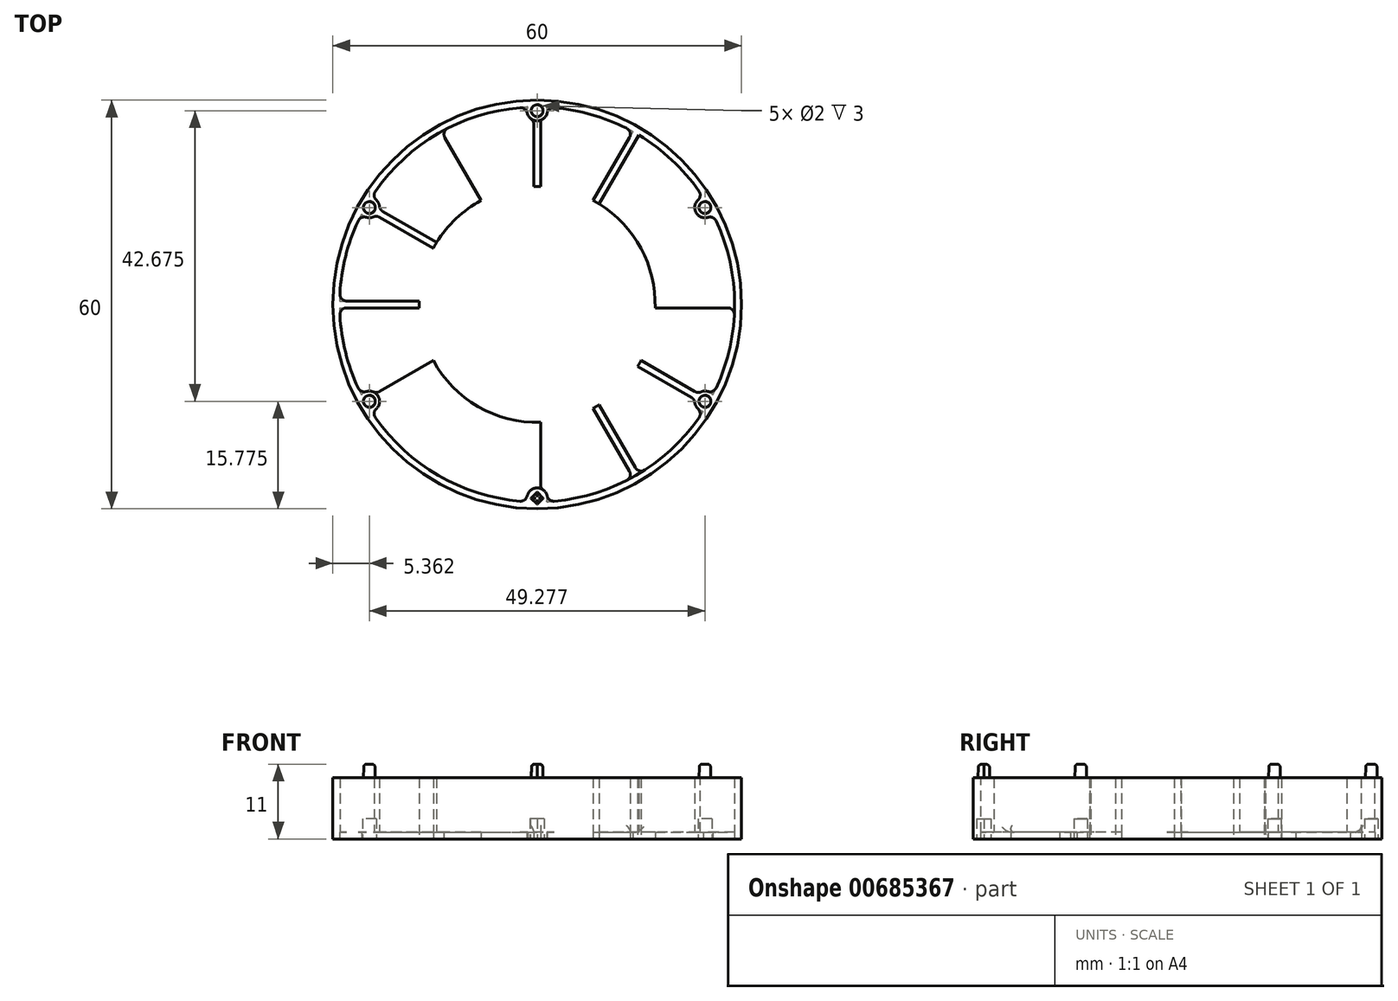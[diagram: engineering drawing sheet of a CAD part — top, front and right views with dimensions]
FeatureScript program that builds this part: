
annotation { "Feature Type Name" : "Feature", "Feature Type Description" : "" }
export const myFeature = defineFeature(function(context is Context, id is Id, definition is map)
    precondition{}
    {
        {
            var Q0;
            Q0=qCreatedBy(makeId("Top.planeOp"),FACE);
            var sketch = newSketch(context, id + "F0", { "sketchPlane" : qUnion([Q0])});
            skCircle(sketch, "E0", {"center": v(0, 0) * mm, "radius": 30 * mm});
            skCircle(sketch, "E1.0", {"center": v(0, 0) * mm, "radius": 29 * mm});
            skLineSegment(sketch, "E2.bottom", {"start": v(14.56, 26.23) * mm, "end": v(15.43, 25.73) * mm});
            skLineSegment(sketch, "E2.top", {"start": v(-15.43, -25.73) * mm, "end": v(-14.56, -26.23) * mm});
            skLineSegment(sketch, "E2.left", {"start": v(14.56, 26.23) * mm, "end": v(-15.43, -25.73) * mm});
            skLineSegment(sketch, "E2.right", {"start": v(15.43, 25.73) * mm, "end": v(-14.56, -26.23) * mm});
            skLineSegment(sketch, "E3.bottom", {"start": v(25.73, 15.43) * mm, "end": v(26.23, 14.56) * mm});
            skLineSegment(sketch, "E3.top", {"start": v(-26.23, -14.56) * mm, "end": v(-25.73, -15.43) * mm});
            skLineSegment(sketch, "E3.left", {"start": v(25.73, 15.43) * mm, "end": v(-26.23, -14.56) * mm});
            skLineSegment(sketch, "E3.right", {"start": v(26.23, 14.56) * mm, "end": v(-25.73, -15.43) * mm});
            skLineSegment(sketch, "E4", {"start": v(-38.35, 0) * mm, "end": v(39.17, 0) * mm, "construction": true});
            skLineSegment(sketch, "E5", {"start": v(0, 42.5) * mm, "end": v(0, -42.47) * mm, "construction": true});
            skLineSegment(sketch, "E6.bottom", {"start": v(-30, 0.5) * mm, "end": v(30, 0.5) * mm});
            skLineSegment(sketch, "E6.top", {"start": v(-30, -0.5) * mm, "end": v(30, -0.5) * mm});
            skLineSegment(sketch, "E6.left", {"start": v(-30, 0.5) * mm, "end": v(-30, -0.5) * mm});
            skLineSegment(sketch, "E6.right", {"start": v(30, 0.5) * mm, "end": v(30, -0.5) * mm});
            skLineSegment(sketch, "E7.bottom", {"start": v(-25.73, 15.43) * mm, "end": v(26.23, -14.56) * mm});
            skLineSegment(sketch, "E7.top", {"start": v(-26.23, 14.56) * mm, "end": v(25.73, -15.43) * mm});
            skLineSegment(sketch, "E7.left", {"start": v(-25.73, 15.43) * mm, "end": v(-26.23, 14.56) * mm});
            skLineSegment(sketch, "E7.right", {"start": v(26.23, -14.56) * mm, "end": v(25.73, -15.43) * mm});
            skLineSegment(sketch, "E8.bottom", {"start": v(-0.5, 30) * mm, "end": v(0.5, 30) * mm});
            skLineSegment(sketch, "E8.top", {"start": v(-0.5, -30) * mm, "end": v(0.5, -30) * mm});
            skLineSegment(sketch, "E8.left", {"start": v(-0.5, 30) * mm, "end": v(-0.5, -30) * mm});
            skLineSegment(sketch, "E8.right", {"start": v(0.5, 30) * mm, "end": v(0.5, -30) * mm});
            skLineSegment(sketch, "E9.bottom", {"start": v(-15.43, 25.73) * mm, "end": v(-14.56, 26.23) * mm});
            skLineSegment(sketch, "E9.top", {"start": v(14.56, -26.23) * mm, "end": v(15.43, -25.73) * mm});
            skLineSegment(sketch, "E9.left", {"start": v(-15.43, 25.73) * mm, "end": v(14.56, -26.23) * mm});
            skLineSegment(sketch, "E9.right", {"start": v(-14.56, 26.23) * mm, "end": v(15.43, -25.73) * mm});
            skCircle(sketch, "E10", {"center": v(0, 0) * mm, "radius": 17.33 * mm});
            skSolve(sketch);
        }
        {
            var Q0;
            Q0=qCreatedBy(makeId("Top.planeOp"),FACE);
            var sketch = newSketch(context, id + "F1", { "sketchPlane" : qUnion([Q0])});
            skCircle(sketch, "E11", {"center": v(0, 0) * mm, "radius": 30 * mm});
            skCircle(sketch, "E12", {"center": v(0, 0) * mm, "radius": 29 * mm});
            skSolve(sketch);
        }
        {
            var Q0;
            Q0=makeQuery(id+"F1.imprint","IMPRINT",FACE,{"disambiguationData":[TD([[makeQuery(id+"F1.imprint","IMPRINT",EDGE,{"derivedFrom":sQuery(id+"F1.wireOp",EDGE,"E11")}),1.0]])]});
            extrude(context, id + "F2", {"entities" : qUnion([Q0]), "depth" : 9 * mm, "offsetDistance" : 25 * mm});
        }
        {
            var Q0;
            {var subQ0=sQuery(id+"F0.wireOp",EDGE,"E7.bottom");var subQ1=sQuery(id+"F0.wireOp",EDGE,"E1.0");var subQ2=makeQuery(id+"F0.imprint","INTERSECT",VERTEX,{"disambiguationData":[OD(0.0)],"derivedFrom":[subQ1,subQ0]});Q0=makeQuery(id+"F0.imprint","IMPRINT",FACE,{"disambiguationData":[TD([[makeQuery(id+"F0.imprint","IMPRINT",EDGE,{"disambiguationData":[TD([[subQ2,-1.0]])],"derivedFrom":subQ1}),1.0]])]});}
            var Q1;
            {var subQ0=sQuery(id+"F0.wireOp",EDGE,"E2.right");var subQ1=sQuery(id+"F0.wireOp",EDGE,"E1.0");var subQ2=makeQuery(id+"F0.imprint","INTERSECT",VERTEX,{"disambiguationData":[OD(0.0)],"derivedFrom":[subQ1,subQ0]});Q1=makeQuery(id+"F0.imprint","IMPRINT",FACE,{"disambiguationData":[TD([[makeQuery(id+"F0.imprint","IMPRINT",EDGE,{"disambiguationData":[TD([[subQ2,-1.0]])],"derivedFrom":subQ1}),1.0]])]});}
            var Q2;
            {var subQ0=sQuery(id+"F0.wireOp",EDGE,"E7.top");var subQ1=sQuery(id+"F0.wireOp",EDGE,"E1.0");var subQ2=makeQuery(id+"F0.imprint","INTERSECT",VERTEX,{"disambiguationData":[OD(1.0)],"derivedFrom":[subQ1,subQ0]});Q2=makeQuery(id+"F0.imprint","IMPRINT",FACE,{"disambiguationData":[TD([[makeQuery(id+"F0.imprint","IMPRINT",EDGE,{"disambiguationData":[TD([[subQ2,-1.0]])],"derivedFrom":subQ1}),1.0]])]});}
            var Q3;
            {var subQ0=sQuery(id+"F0.wireOp",EDGE,"E6.bottom");var subQ1=sQuery(id+"F0.wireOp",EDGE,"E1.0");var subQ2=makeQuery(id+"F0.imprint","INTERSECT",VERTEX,{"disambiguationData":[OD(1.0)],"derivedFrom":[subQ1,subQ0]});Q3=makeQuery(id+"F0.imprint","IMPRINT",FACE,{"disambiguationData":[TD([[makeQuery(id+"F0.imprint","IMPRINT",EDGE,{"disambiguationData":[TD([[subQ2,-1.0]])],"derivedFrom":subQ1}),1.0]])]});}
            extrude(context, id + "F3", {"entities" : qUnion([Q0, Q1, Q2, Q3]), "operationType" : NewBodyOperationType.ADD, "depth" : 9 * mm, "offsetDistance" : 25 * mm});
        }
        {
            var Q0;
            Q0=makeQuery(id+"F1.imprint","IMPRINT",FACE,{"disambiguationData":[TD([[makeQuery(id+"F1.imprint","IMPRINT",EDGE,{"derivedFrom":sQuery(id+"F1.wireOp",EDGE,"E11")}),1.0]])]});
            var Q1;
            Q1=makeQuery(id+"F1.imprint","IMPRINT",FACE,{"disambiguationData":[TD([[makeQuery(id+"F1.imprint","IMPRINT",EDGE,{"derivedFrom":sQuery(id+"F1.wireOp",EDGE,"E12")}),1.0]])]});
            extrude(context, id + "F4", {"entities" : qUnion([Q0, Q1]), "operationType" : NewBodyOperationType.ADD, "depth" : 1 * mm, "offsetDistance" : 25 * mm});
        }
        {
            var Q0;
            {var subQ0=sQuery(id+"F0.wireOp",EDGE,"E8.right");var subQ1=sQuery(id+"F0.wireOp",EDGE,"E1.0");var subQ2=makeQuery(id+"F0.imprint","INTERSECT",VERTEX,{"disambiguationData":[OD(1.0)],"derivedFrom":[subQ1,subQ0]});Q0=makeQuery(id+"F0.imprint","IMPRINT",FACE,{"disambiguationData":[TD([[makeQuery(id+"F0.imprint","IMPRINT",EDGE,{"disambiguationData":[TD([[subQ2,-1.0]])],"derivedFrom":subQ1}),1.0]])]});}
            var Q1;
            {var subQ0=sQuery(id+"F0.wireOp",EDGE,"E9.right");var subQ1=sQuery(id+"F0.wireOp",EDGE,"E1.0");var subQ2=makeQuery(id+"F0.imprint","INTERSECT",VERTEX,{"disambiguationData":[OD(1.0)],"derivedFrom":[subQ1,subQ0]});Q1=makeQuery(id+"F0.imprint","IMPRINT",FACE,{"disambiguationData":[TD([[makeQuery(id+"F0.imprint","IMPRINT",EDGE,{"disambiguationData":[TD([[subQ2,-1.0]])],"derivedFrom":subQ1}),1.0]])]});}
            var Q2;
            {var subQ0=sQuery(id+"F0.wireOp",EDGE,"E7.bottom");var subQ1=sQuery(id+"F0.wireOp",EDGE,"E1.0");var subQ2=makeQuery(id+"F0.imprint","INTERSECT",VERTEX,{"disambiguationData":[OD(1.0)],"derivedFrom":[subQ1,subQ0]});Q2=makeQuery(id+"F0.imprint","IMPRINT",FACE,{"disambiguationData":[TD([[makeQuery(id+"F0.imprint","IMPRINT",EDGE,{"disambiguationData":[TD([[subQ2,-1.0]])],"derivedFrom":subQ1}),1.0]])]});}
            var Q3;
            {var subQ0=sQuery(id+"F0.wireOp",EDGE,"E2.left");var subQ1=sQuery(id+"F0.wireOp",EDGE,"E1.0");var subQ2=makeQuery(id+"F0.imprint","INTERSECT",VERTEX,{"disambiguationData":[OD(0.0)],"derivedFrom":[subQ1,subQ0]});Q3=makeQuery(id+"F0.imprint","IMPRINT",FACE,{"disambiguationData":[TD([[makeQuery(id+"F0.imprint","IMPRINT",EDGE,{"disambiguationData":[TD([[subQ2,-1.0]])],"derivedFrom":subQ1}),1.0]])]});}
            var Q4;
            {var subQ0=sQuery(id+"F0.wireOp",EDGE,"E8.left");var subQ1=sQuery(id+"F0.wireOp",EDGE,"E1.0");var subQ2=makeQuery(id+"F0.imprint","INTERSECT",VERTEX,{"disambiguationData":[OD(0.0)],"derivedFrom":[subQ1,subQ0]});Q4=makeQuery(id+"F0.imprint","IMPRINT",FACE,{"disambiguationData":[TD([[makeQuery(id+"F0.imprint","IMPRINT",EDGE,{"disambiguationData":[TD([[subQ2,-1.0]])],"derivedFrom":subQ1}),1.0]])]});}
            var Q5;
            {var subQ0=sQuery(id+"F0.wireOp",EDGE,"E7.top");var subQ1=sQuery(id+"F0.wireOp",EDGE,"E1.0");var subQ2=makeQuery(id+"F0.imprint","INTERSECT",VERTEX,{"disambiguationData":[OD(0.0)],"derivedFrom":[subQ1,subQ0]});Q5=makeQuery(id+"F0.imprint","IMPRINT",FACE,{"disambiguationData":[TD([[makeQuery(id+"F0.imprint","IMPRINT",EDGE,{"disambiguationData":[TD([[subQ2,-1.0]])],"derivedFrom":subQ1}),1.0]])]});}
            var Q6;
            {var subQ0=sQuery(id+"F0.wireOp",EDGE,"E6.top");var subQ1=sQuery(id+"F0.wireOp",EDGE,"E1.0");var subQ2=makeQuery(id+"F0.imprint","INTERSECT",VERTEX,{"disambiguationData":[OD(0.0)],"derivedFrom":[subQ1,subQ0]});Q6=makeQuery(id+"F0.imprint","IMPRINT",FACE,{"disambiguationData":[TD([[makeQuery(id+"F0.imprint","IMPRINT",EDGE,{"disambiguationData":[TD([[subQ2,-1.0]])],"derivedFrom":subQ1}),1.0]])]});}
            extrude(context, id + "F5", {"entities" : qUnion([Q0, Q1, Q2, Q3, Q4, Q5, Q6]), "operationType" : NewBodyOperationType.REMOVE, "depth" : 1 * mm, "offsetDistance" : 25 * mm});
        }
        {
            var Q0;
            Q0=qCreatedBy(makeId("Top.planeOp"),FACE);
            var sketch = newSketch(context, id + "F6", { "sketchPlane" : qUnion([Q0])});
            skCircle(sketch, "E13", {"center": v(0, 0) * mm, "radius": 28.45 * mm});
            skLineSegment(sketch, "E14", {"start": v(0, 28.45) * mm, "end": v(0, -28.45) * mm, "construction": true});
            skLineSegment(sketch, "E15", {"start": v(24.64, 14.22) * mm, "end": v(0, 0) * mm, "construction": true});
            skLineSegment(sketch, "E16", {"start": v(14.23, 24.64) * mm, "end": v(0, 0) * mm, "construction": true});
            skLineSegment(sketch, "E17", {"start": v(0, 0) * mm, "end": v(28.45, 0) * mm, "construction": true});
            skLineSegment(sketch, "E18", {"start": v(0, 0) * mm, "end": v(24.64, -14.22) * mm, "construction": true});
            skLineSegment(sketch, "E19", {"start": v(0, 0) * mm, "end": v(14.23, -24.64) * mm, "construction": true});
            skLineSegment(sketch, "E20", {"start": v(0, 0) * mm, "end": v(-14.23, 24.64) * mm, "construction": true});
            skLineSegment(sketch, "E21", {"start": v(0, 0) * mm, "end": v(-24.64, 14.22) * mm, "construction": true});
            skLineSegment(sketch, "E22", {"start": v(0, 0) * mm, "end": v(-28.45, 0) * mm, "construction": true});
            skLineSegment(sketch, "E23", {"start": v(0, 0) * mm, "end": v(-24.64, -14.23) * mm, "construction": true});
            skLineSegment(sketch, "E24", {"start": v(0, 0) * mm, "end": v(-14.22, -24.64) * mm, "construction": true});
            skCircle(sketch, "E25", {"center": v(0, 28.45) * mm, "radius": 1.5 * mm});
            skCircle(sketch, "E26", {"center": v(24.64, 14.22) * mm, "radius": 1.5 * mm});
            skCircle(sketch, "E27", {"center": v(24.64, -14.22) * mm, "radius": 1.5 * mm});
            skCircle(sketch, "E28", {"center": v(0, -28.45) * mm, "radius": 1.5 * mm});
            skCircle(sketch, "E29", {"center": v(-24.64, -14.23) * mm, "radius": 1.5 * mm});
            skCircle(sketch, "E30", {"center": v(-24.64, 14.22) * mm, "radius": 1.5 * mm});
            skCircle(sketch, "E31", {"center": v(-24.64, 14.22) * mm, "radius": 1 * mm});
            skCircle(sketch, "E32", {"center": v(0, 28.45) * mm, "radius": 1 * mm});
            skCircle(sketch, "E33", {"center": v(24.64, 14.22) * mm, "radius": 1 * mm});
            skCircle(sketch, "E34", {"center": v(24.64, -14.22) * mm, "radius": 1 * mm});
            skCircle(sketch, "E35", {"center": v(-24.64, -14.23) * mm, "radius": 1 * mm});
            skLineSegment(sketch, "E36.bottom", {"start": v(1.06, -28.45) * mm, "end": v(0, -29.51) * mm});
            skLineSegment(sketch, "E36.top", {"start": v(0, -27.39) * mm, "end": v(-1.06, -28.45) * mm});
            skLineSegment(sketch, "E36.left", {"start": v(1.06, -28.45) * mm, "end": v(0, -27.39) * mm});
            skLineSegment(sketch, "E36.right", {"start": v(0, -29.51) * mm, "end": v(-1.06, -28.45) * mm});
            skSolve(sketch);
        }
        {
            var Q0;
            {var subQ0=sQuery(id+"F6.wireOp",EDGE,"E30");var subQ1=sQuery(id+"F6.wireOp",EDGE,"E13");var subQ2=makeQuery(id+"F6.imprint","INTERSECT",VERTEX,{"disambiguationData":[OD(0.0)],"derivedFrom":[subQ1,subQ0]});Q0=makeQuery(id+"F6.imprint","IMPRINT",FACE,{"disambiguationData":[TD([[makeQuery(id+"F6.imprint","IMPRINT",EDGE,{"disambiguationData":[TD([[subQ2,-1.0]])],"derivedFrom":subQ1}),1.0]])]});}
            var Q1;
            {var subQ0=sQuery(id+"F6.wireOp",EDGE,"E30");var subQ1=sQuery(id+"F6.wireOp",EDGE,"E13");var subQ2=makeQuery(id+"F6.imprint","INTERSECT",VERTEX,{"disambiguationData":[OD(0.0)],"derivedFrom":[subQ1,subQ0]});Q1=makeQuery(id+"F6.imprint","IMPRINT",FACE,{"disambiguationData":[TD([[makeQuery(id+"F6.imprint","IMPRINT",EDGE,{"disambiguationData":[TD([[subQ2,-1.0]])],"derivedFrom":subQ1}),-1.0]])]});}
            var Q2;
            {var subQ0=sQuery(id+"F6.wireOp",EDGE,"E25");var subQ1=sQuery(id+"F6.wireOp",EDGE,"E13");var subQ2=makeQuery(id+"F6.imprint","INTERSECT",VERTEX,{"disambiguationData":[OD(0.0)],"derivedFrom":[subQ1,subQ0]});Q2=makeQuery(id+"F6.imprint","IMPRINT",FACE,{"disambiguationData":[TD([[makeQuery(id+"F6.imprint","IMPRINT",EDGE,{"disambiguationData":[TD([[subQ2,-1.0]])],"derivedFrom":subQ1}),1.0]])]});}
            var Q3;
            {var subQ0=sQuery(id+"F6.wireOp",EDGE,"E25");var subQ1=sQuery(id+"F6.wireOp",EDGE,"E13");var subQ2=makeQuery(id+"F6.imprint","INTERSECT",VERTEX,{"disambiguationData":[OD(0.0)],"derivedFrom":[subQ1,subQ0]});Q3=makeQuery(id+"F6.imprint","IMPRINT",FACE,{"disambiguationData":[TD([[makeQuery(id+"F6.imprint","IMPRINT",EDGE,{"disambiguationData":[TD([[subQ2,-1.0]])],"derivedFrom":subQ1}),-1.0]])]});}
            var Q4;
            {var subQ0=sQuery(id+"F6.wireOp",EDGE,"E26");var subQ1=sQuery(id+"F6.wireOp",EDGE,"E13");var subQ2=makeQuery(id+"F6.imprint","INTERSECT",VERTEX,{"disambiguationData":[OD(0.0)],"derivedFrom":[subQ1,subQ0]});Q4=makeQuery(id+"F6.imprint","IMPRINT",FACE,{"disambiguationData":[TD([[makeQuery(id+"F6.imprint","IMPRINT",EDGE,{"disambiguationData":[TD([[subQ2,-1.0]])],"derivedFrom":subQ1}),-1.0]])]});}
            var Q5;
            {var subQ0=sQuery(id+"F6.wireOp",EDGE,"E26");var subQ1=sQuery(id+"F6.wireOp",EDGE,"E13");var subQ2=makeQuery(id+"F6.imprint","INTERSECT",VERTEX,{"disambiguationData":[OD(0.0)],"derivedFrom":[subQ1,subQ0]});Q5=makeQuery(id+"F6.imprint","IMPRINT",FACE,{"disambiguationData":[TD([[makeQuery(id+"F6.imprint","IMPRINT",EDGE,{"disambiguationData":[TD([[subQ2,-1.0]])],"derivedFrom":subQ1}),1.0]])]});}
            var Q6;
            {var subQ0=sQuery(id+"F6.wireOp",EDGE,"E29");var subQ1=sQuery(id+"F6.wireOp",EDGE,"E13");var subQ2=makeQuery(id+"F6.imprint","INTERSECT",VERTEX,{"disambiguationData":[OD(0.0)],"derivedFrom":[subQ1,subQ0]});Q6=makeQuery(id+"F6.imprint","IMPRINT",FACE,{"disambiguationData":[TD([[makeQuery(id+"F6.imprint","IMPRINT",EDGE,{"disambiguationData":[TD([[subQ2,-1.0]])],"derivedFrom":subQ1}),1.0]])]});}
            var Q7;
            {var subQ0=sQuery(id+"F6.wireOp",EDGE,"E29");var subQ1=sQuery(id+"F6.wireOp",EDGE,"E13");var subQ2=makeQuery(id+"F6.imprint","INTERSECT",VERTEX,{"disambiguationData":[OD(0.0)],"derivedFrom":[subQ1,subQ0]});Q7=makeQuery(id+"F6.imprint","IMPRINT",FACE,{"disambiguationData":[TD([[makeQuery(id+"F6.imprint","IMPRINT",EDGE,{"disambiguationData":[TD([[subQ2,-1.0]])],"derivedFrom":subQ1}),-1.0]])]});}
            var Q8;
            {var subQ3=sQuery(id+"F6.wireOp",EDGE,"E13");var subQ5=sQuery(id+"F6.wireOp",EDGE,"E28");var subQ6=makeQuery(id+"F6.imprint","INTERSECT",VERTEX,{"disambiguationData":[OD(0.0)],"derivedFrom":[subQ3,subQ5]});Q8=makeQuery(id+"F6.imprint","IMPRINT",FACE,{"disambiguationData":[TD([[makeQuery(id+"F6.imprint","IMPRINT",EDGE,{"disambiguationData":[TD([[subQ6,-1.0]])],"derivedFrom":subQ3}),1.0]])]});}
            var Q9;
            {var subQ6=sQuery(id+"F6.wireOp",EDGE,"E36.bottom");Q9=makeQuery(id+"F6.imprint","IMPRINT",FACE,{"disambiguationData":[TD([[makeQuery(id+"F6.imprint","IMPRINT",EDGE,{"derivedFrom":subQ6}),1.0]])]});}
            var Q10;
            {var subQ0=sQuery(id+"F6.wireOp",EDGE,"E27");var subQ1=sQuery(id+"F6.wireOp",EDGE,"E13");var subQ2=makeQuery(id+"F6.imprint","INTERSECT",VERTEX,{"disambiguationData":[OD(0.0)],"derivedFrom":[subQ1,subQ0]});Q10=makeQuery(id+"F6.imprint","IMPRINT",FACE,{"disambiguationData":[TD([[makeQuery(id+"F6.imprint","IMPRINT",EDGE,{"disambiguationData":[TD([[subQ2,-1.0]])],"derivedFrom":subQ1}),-1.0]])]});}
            var Q11;
            {var subQ0=sQuery(id+"F6.wireOp",EDGE,"E27");var subQ1=sQuery(id+"F6.wireOp",EDGE,"E13");var subQ2=makeQuery(id+"F6.imprint","INTERSECT",VERTEX,{"disambiguationData":[OD(0.0)],"derivedFrom":[subQ1,subQ0]});Q11=makeQuery(id+"F6.imprint","IMPRINT",FACE,{"disambiguationData":[TD([[makeQuery(id+"F6.imprint","IMPRINT",EDGE,{"disambiguationData":[TD([[subQ2,-1.0]])],"derivedFrom":subQ1}),1.0]])]});}
            var Q12;
            {var subQ0=sQuery(id+"F6.wireOp",EDGE,"E31");var subQ1=sQuery(id+"F6.wireOp",EDGE,"E13");var subQ2=makeQuery(id+"F6.imprint","INTERSECT",VERTEX,{"disambiguationData":[OD(0.0)],"derivedFrom":[subQ1,subQ0]});Q12=makeQuery(id+"F6.imprint","IMPRINT",FACE,{"disambiguationData":[TD([[makeQuery(id+"F6.imprint","IMPRINT",EDGE,{"disambiguationData":[TD([[subQ2,-1.0]])],"derivedFrom":subQ1}),1.0]])]});}
            var Q13;
            {var subQ0=sQuery(id+"F6.wireOp",EDGE,"E31");var subQ1=sQuery(id+"F6.wireOp",EDGE,"E13");var subQ2=makeQuery(id+"F6.imprint","INTERSECT",VERTEX,{"disambiguationData":[OD(0.0)],"derivedFrom":[subQ1,subQ0]});Q13=makeQuery(id+"F6.imprint","IMPRINT",FACE,{"disambiguationData":[TD([[makeQuery(id+"F6.imprint","IMPRINT",EDGE,{"disambiguationData":[TD([[subQ2,-1.0]])],"derivedFrom":subQ1}),-1.0]])]});}
            var Q14;
            {var subQ0=sQuery(id+"F6.wireOp",EDGE,"E32");var subQ1=sQuery(id+"F6.wireOp",EDGE,"E13");var subQ2=makeQuery(id+"F6.imprint","INTERSECT",VERTEX,{"disambiguationData":[OD(0.0)],"derivedFrom":[subQ1,subQ0]});Q14=makeQuery(id+"F6.imprint","IMPRINT",FACE,{"disambiguationData":[TD([[makeQuery(id+"F6.imprint","IMPRINT",EDGE,{"disambiguationData":[TD([[subQ2,-1.0]])],"derivedFrom":subQ1}),-1.0]])]});}
            var Q15;
            {var subQ0=sQuery(id+"F6.wireOp",EDGE,"E32");var subQ1=sQuery(id+"F6.wireOp",EDGE,"E13");var subQ2=makeQuery(id+"F6.imprint","INTERSECT",VERTEX,{"disambiguationData":[OD(0.0)],"derivedFrom":[subQ1,subQ0]});Q15=makeQuery(id+"F6.imprint","IMPRINT",FACE,{"disambiguationData":[TD([[makeQuery(id+"F6.imprint","IMPRINT",EDGE,{"disambiguationData":[TD([[subQ2,-1.0]])],"derivedFrom":subQ1}),1.0]])]});}
            var Q16;
            {var subQ0=sQuery(id+"F6.wireOp",EDGE,"E33");var subQ1=sQuery(id+"F6.wireOp",EDGE,"E13");var subQ2=makeQuery(id+"F6.imprint","INTERSECT",VERTEX,{"disambiguationData":[OD(0.0)],"derivedFrom":[subQ1,subQ0]});Q16=makeQuery(id+"F6.imprint","IMPRINT",FACE,{"disambiguationData":[TD([[makeQuery(id+"F6.imprint","IMPRINT",EDGE,{"disambiguationData":[TD([[subQ2,-1.0]])],"derivedFrom":subQ1}),-1.0]])]});}
            var Q17;
            {var subQ0=sQuery(id+"F6.wireOp",EDGE,"E33");var subQ1=sQuery(id+"F6.wireOp",EDGE,"E13");var subQ2=makeQuery(id+"F6.imprint","INTERSECT",VERTEX,{"disambiguationData":[OD(0.0)],"derivedFrom":[subQ1,subQ0]});Q17=makeQuery(id+"F6.imprint","IMPRINT",FACE,{"disambiguationData":[TD([[makeQuery(id+"F6.imprint","IMPRINT",EDGE,{"disambiguationData":[TD([[subQ2,-1.0]])],"derivedFrom":subQ1}),1.0]])]});}
            var Q18;
            {var subQ0=sQuery(id+"F6.wireOp",EDGE,"E34");var subQ1=sQuery(id+"F6.wireOp",EDGE,"E13");var subQ2=makeQuery(id+"F6.imprint","INTERSECT",VERTEX,{"disambiguationData":[OD(0.0)],"derivedFrom":[subQ1,subQ0]});Q18=makeQuery(id+"F6.imprint","IMPRINT",FACE,{"disambiguationData":[TD([[makeQuery(id+"F6.imprint","IMPRINT",EDGE,{"disambiguationData":[TD([[subQ2,-1.0]])],"derivedFrom":subQ1}),-1.0]])]});}
            var Q19;
            {var subQ0=sQuery(id+"F6.wireOp",EDGE,"E34");var subQ1=sQuery(id+"F6.wireOp",EDGE,"E13");var subQ2=makeQuery(id+"F6.imprint","INTERSECT",VERTEX,{"disambiguationData":[OD(0.0)],"derivedFrom":[subQ1,subQ0]});Q19=makeQuery(id+"F6.imprint","IMPRINT",FACE,{"disambiguationData":[TD([[makeQuery(id+"F6.imprint","IMPRINT",EDGE,{"disambiguationData":[TD([[subQ2,-1.0]])],"derivedFrom":subQ1}),1.0]])]});}
            var Q20;
            {var subQ1=sQuery(id+"F6.wireOp",EDGE,"E36.bottom");Q20=makeQuery(id+"F6.imprint","IMPRINT",FACE,{"disambiguationData":[TD([[makeQuery(id+"F6.imprint","IMPRINT",EDGE,{"derivedFrom":subQ1}),-1.0]])]});}
            var Q21;
            {var subQ0=sQuery(id+"F6.wireOp",EDGE,"E35");var subQ1=sQuery(id+"F6.wireOp",EDGE,"E13");var subQ2=makeQuery(id+"F6.imprint","INTERSECT",VERTEX,{"disambiguationData":[OD(0.0)],"derivedFrom":[subQ1,subQ0]});Q21=makeQuery(id+"F6.imprint","IMPRINT",FACE,{"disambiguationData":[TD([[makeQuery(id+"F6.imprint","IMPRINT",EDGE,{"disambiguationData":[TD([[subQ2,-1.0]])],"derivedFrom":subQ1}),-1.0]])]});}
            var Q22;
            {var subQ0=sQuery(id+"F6.wireOp",EDGE,"E35");var subQ1=sQuery(id+"F6.wireOp",EDGE,"E13");var subQ2=makeQuery(id+"F6.imprint","INTERSECT",VERTEX,{"disambiguationData":[OD(0.0)],"derivedFrom":[subQ1,subQ0]});Q22=makeQuery(id+"F6.imprint","IMPRINT",FACE,{"disambiguationData":[TD([[makeQuery(id+"F6.imprint","IMPRINT",EDGE,{"disambiguationData":[TD([[subQ2,-1.0]])],"derivedFrom":subQ1}),1.0]])]});}
            var Q23;
            {var subQ0=sQuery(id+"F6.wireOp",EDGE,"E36.top");var subQ1=sQuery(id+"F6.wireOp",EDGE,"E13");var subQ2=makeQuery(id+"F6.imprint","INTERSECT",VERTEX,{"derivedFrom":[subQ1,subQ0]});Q23=makeQuery(id+"F6.imprint","IMPRINT",FACE,{"disambiguationData":[TD([[makeQuery(id+"F6.imprint","IMPRINT",EDGE,{"disambiguationData":[TD([[subQ2,-1.0]])],"derivedFrom":subQ1}),1.0]])]});}
            extrude(context, id + "F7", {"entities" : qUnion([Q0, Q1, Q2, Q3, Q4, Q5, Q6, Q7, Q8, Q9, Q10, Q11, Q12, Q13, Q14, Q15, Q16, Q17, Q18, Q19, Q20, Q21, Q22, Q23]), "operationType" : NewBodyOperationType.ADD, "depth" : 9 * mm, "offsetDistance" : 25 * mm});
        }
        {
            var Q0;
            {var subQ0=sQuery(id+"F0.wireOp",EDGE,"E8.right");var subQ1=sQuery(id+"F0.wireOp",EDGE,"E1.0");Q0=makeQuery(id+"F3.opExtrude","SWEPT_EDGE",EDGE,{"disambiguationData":[OSD([subQ1,subQ0]),TDD([makeQuery(id+"F0.imprint","INTERSECT",VERTEX,{"disambiguationData":[OD(1.0)],"derivedFrom":[subQ1,subQ0]})])]});}
            var Q1;
            {var subQ0=sQuery(id+"F0.wireOp",EDGE,"E2.left");var subQ1=sQuery(id+"F0.wireOp",EDGE,"E1.0");Q1=makeQuery(id+"F3.opExtrude","SWEPT_EDGE",EDGE,{"disambiguationData":[OSD([subQ1,subQ0]),TDD([makeQuery(id+"F0.imprint","INTERSECT",VERTEX,{"disambiguationData":[OD(1.0)],"derivedFrom":[subQ1,subQ0]})])]});}
            var Q2;
            {var subQ0=sQuery(id+"F0.wireOp",EDGE,"E3.left");var subQ1=sQuery(id+"F0.wireOp",EDGE,"E1.0");Q2=makeQuery(id+"F3.opExtrude","SWEPT_EDGE",EDGE,{"disambiguationData":[OSD([subQ1,subQ0]),TDD([makeQuery(id+"F0.imprint","INTERSECT",VERTEX,{"disambiguationData":[OD(1.0)],"derivedFrom":[subQ1,subQ0]})])]});}
            var Q3;
            {var subQ0=sQuery(id+"F0.wireOp",EDGE,"E6.bottom");var subQ1=sQuery(id+"F0.wireOp",EDGE,"E1.0");Q3=makeQuery(id+"F3.opExtrude","SWEPT_EDGE",EDGE,{"disambiguationData":[OSD([subQ1,subQ0]),TDD([makeQuery(id+"F0.imprint","INTERSECT",VERTEX,{"disambiguationData":[OD(1.0)],"derivedFrom":[subQ1,subQ0]})])]});}
            var Q4;
            {var subQ0=sQuery(id+"F0.wireOp",EDGE,"E9.right");var subQ1=sQuery(id+"F0.wireOp",EDGE,"E1.0");Q4=makeQuery(id+"F3.opExtrude","SWEPT_EDGE",EDGE,{"disambiguationData":[OSD([subQ1,subQ0]),TDD([makeQuery(id+"F0.imprint","INTERSECT",VERTEX,{"disambiguationData":[OD(1.0)],"derivedFrom":[subQ1,subQ0]})])]});}
            var Q5;
            {var subQ0=sQuery(id+"F0.wireOp",EDGE,"E7.bottom");var subQ1=sQuery(id+"F0.wireOp",EDGE,"E1.0");Q5=makeQuery(id+"F3.opExtrude","SWEPT_EDGE",EDGE,{"disambiguationData":[OSD([subQ1,subQ0]),TDD([makeQuery(id+"F0.imprint","INTERSECT",VERTEX,{"disambiguationData":[OD(1.0)],"derivedFrom":[subQ1,subQ0]})])]});}
            var Q6;
            {var subQ0=sQuery(id+"F0.wireOp",EDGE,"E8.left");var subQ1=sQuery(id+"F0.wireOp",EDGE,"E1.0");Q6=makeQuery(id+"F3.opExtrude","SWEPT_EDGE",EDGE,{"disambiguationData":[OSD([subQ1,subQ0]),TDD([makeQuery(id+"F0.imprint","INTERSECT",VERTEX,{"disambiguationData":[OD(0.0)],"derivedFrom":[subQ1,subQ0]})])]});}
            var Q7;
            {var subQ0=sQuery(id+"F0.wireOp",EDGE,"E2.left");var subQ1=sQuery(id+"F0.wireOp",EDGE,"E1.0");Q7=makeQuery(id+"F3.opExtrude","SWEPT_EDGE",EDGE,{"disambiguationData":[OSD([subQ1,subQ0]),TDD([makeQuery(id+"F0.imprint","INTERSECT",VERTEX,{"disambiguationData":[OD(0.0)],"derivedFrom":[subQ1,subQ0]})])]});}
            var Q8;
            {var subQ0=sQuery(id+"F0.wireOp",EDGE,"E3.left");var subQ1=sQuery(id+"F0.wireOp",EDGE,"E1.0");Q8=makeQuery(id+"F3.opExtrude","SWEPT_EDGE",EDGE,{"disambiguationData":[OSD([subQ1,subQ0]),TDD([makeQuery(id+"F0.imprint","INTERSECT",VERTEX,{"disambiguationData":[OD(0.0)],"derivedFrom":[subQ1,subQ0]})])]});}
            var Q9;
            {var subQ0=sQuery(id+"F0.wireOp",EDGE,"E6.top");var subQ1=sQuery(id+"F0.wireOp",EDGE,"E1.0");Q9=makeQuery(id+"F3.opExtrude","SWEPT_EDGE",EDGE,{"disambiguationData":[OSD([subQ1,subQ0]),TDD([makeQuery(id+"F0.imprint","INTERSECT",VERTEX,{"disambiguationData":[OD(1.0)],"derivedFrom":[subQ1,subQ0]})])]});}
            var Q10;
            {var subQ0=sQuery(id+"F0.wireOp",EDGE,"E7.top");var subQ1=sQuery(id+"F0.wireOp",EDGE,"E1.0");Q10=makeQuery(id+"F3.opExtrude","SWEPT_EDGE",EDGE,{"disambiguationData":[OSD([subQ1,subQ0]),TDD([makeQuery(id+"F0.imprint","INTERSECT",VERTEX,{"disambiguationData":[OD(0.0)],"derivedFrom":[subQ1,subQ0]})])]});}
            var Q11;
            {var subQ0=sQuery(id+"F0.wireOp",EDGE,"E6.top");var subQ1=sQuery(id+"F0.wireOp",EDGE,"E1.0");Q11=makeQuery(id+"F3.opExtrude","SWEPT_EDGE",EDGE,{"disambiguationData":[OSD([subQ1,subQ0]),TDD([makeQuery(id+"F0.imprint","INTERSECT",VERTEX,{"disambiguationData":[OD(0.0)],"derivedFrom":[subQ1,subQ0]})])]});}
            var Q12;
            {var subQ0=sQuery(id+"F0.wireOp",EDGE,"E9.left");var subQ1=sQuery(id+"F0.wireOp",EDGE,"E1.0");Q12=makeQuery(id+"F3.opExtrude","SWEPT_EDGE",EDGE,{"disambiguationData":[OSD([subQ1,subQ0]),TDD([makeQuery(id+"F0.imprint","INTERSECT",VERTEX,{"disambiguationData":[OD(0.0)],"derivedFrom":[subQ1,subQ0]})])]});}
            var Q13;
            {var subQ0=sQuery(id+"F0.wireOp",EDGE,"E8.right");var subQ1=sQuery(id+"F0.wireOp",EDGE,"E1.0");Q13=makeQuery(id+"F3.opExtrude","SWEPT_EDGE",EDGE,{"disambiguationData":[OSD([subQ1,subQ0]),TDD([makeQuery(id+"F0.imprint","INTERSECT",VERTEX,{"disambiguationData":[OD(0.0)],"derivedFrom":[subQ1,subQ0]})])]});}
            var Q14;
            {var subQ0=sQuery(id+"F0.wireOp",EDGE,"E7.bottom");var subQ1=sQuery(id+"F0.wireOp",EDGE,"E1.0");Q14=makeQuery(id+"F3.opExtrude","SWEPT_EDGE",EDGE,{"disambiguationData":[OSD([subQ1,subQ0]),TDD([makeQuery(id+"F0.imprint","INTERSECT",VERTEX,{"disambiguationData":[OD(0.0)],"derivedFrom":[subQ1,subQ0]})])]});}
            var Q15;
            {var subQ0=sQuery(id+"F0.wireOp",EDGE,"E9.right");var subQ1=sQuery(id+"F0.wireOp",EDGE,"E1.0");Q15=makeQuery(id+"F3.opExtrude","SWEPT_EDGE",EDGE,{"disambiguationData":[OSD([subQ1,subQ0]),TDD([makeQuery(id+"F0.imprint","INTERSECT",VERTEX,{"disambiguationData":[OD(0.0)],"derivedFrom":[subQ1,subQ0]})])]});}
            var Q16;
            {var subQ0=sQuery(id+"F0.wireOp",EDGE,"E3.right");var subQ1=sQuery(id+"F0.wireOp",EDGE,"E1.0");Q16=makeQuery(id+"F3.opExtrude","SWEPT_EDGE",EDGE,{"disambiguationData":[OSD([subQ1,subQ0]),TDD([makeQuery(id+"F0.imprint","INTERSECT",VERTEX,{"disambiguationData":[OD(1.0)],"derivedFrom":[subQ1,subQ0]})])]});}
            var Q17;
            {var subQ0=sQuery(id+"F0.wireOp",EDGE,"E2.right");var subQ1=sQuery(id+"F0.wireOp",EDGE,"E1.0");Q17=makeQuery(id+"F3.opExtrude","SWEPT_EDGE",EDGE,{"disambiguationData":[OSD([subQ1,subQ0]),TDD([makeQuery(id+"F0.imprint","INTERSECT",VERTEX,{"disambiguationData":[OD(1.0)],"derivedFrom":[subQ1,subQ0]})])]});}
            var Q18;
            {var subQ0=sQuery(id+"F0.wireOp",EDGE,"E3.right");var subQ1=sQuery(id+"F0.wireOp",EDGE,"E1.0");Q18=makeQuery(id+"F3.opExtrude","SWEPT_EDGE",EDGE,{"disambiguationData":[OSD([subQ1,subQ0]),TDD([makeQuery(id+"F0.imprint","INTERSECT",VERTEX,{"disambiguationData":[OD(0.0)],"derivedFrom":[subQ1,subQ0]})])]});}
            var Q19;
            {var subQ0=sQuery(id+"F0.wireOp",EDGE,"E2.right");var subQ1=sQuery(id+"F0.wireOp",EDGE,"E1.0");Q19=makeQuery(id+"F3.opExtrude","SWEPT_EDGE",EDGE,{"disambiguationData":[OSD([subQ1,subQ0]),TDD([makeQuery(id+"F0.imprint","INTERSECT",VERTEX,{"disambiguationData":[OD(0.0)],"derivedFrom":[subQ1,subQ0]})])]});}
            var Q20;
            {var subQ0=sQuery(id+"F0.wireOp",EDGE,"E8.left");var subQ1=sQuery(id+"F0.wireOp",EDGE,"E1.0");Q20=makeQuery(id+"F3.opExtrude","SWEPT_EDGE",EDGE,{"disambiguationData":[OSD([subQ1,subQ0]),TDD([makeQuery(id+"F0.imprint","INTERSECT",VERTEX,{"disambiguationData":[OD(1.0)],"derivedFrom":[subQ1,subQ0]})])]});}
            var Q21;
            {var subQ0=sQuery(id+"F0.wireOp",EDGE,"E9.left");var subQ1=sQuery(id+"F0.wireOp",EDGE,"E1.0");Q21=makeQuery(id+"F3.opExtrude","SWEPT_EDGE",EDGE,{"disambiguationData":[OSD([subQ1,subQ0]),TDD([makeQuery(id+"F0.imprint","INTERSECT",VERTEX,{"disambiguationData":[OD(1.0)],"derivedFrom":[subQ1,subQ0]})])]});}
            var Q22;
            {var subQ0=sQuery(id+"F0.wireOp",EDGE,"E7.top");var subQ1=sQuery(id+"F0.wireOp",EDGE,"E1.0");Q22=makeQuery(id+"F3.opExtrude","SWEPT_EDGE",EDGE,{"disambiguationData":[OSD([subQ1,subQ0]),TDD([makeQuery(id+"F0.imprint","INTERSECT",VERTEX,{"disambiguationData":[OD(1.0)],"derivedFrom":[subQ1,subQ0]})])]});}
            var Q23;
            {var subQ0=sQuery(id+"F0.wireOp",EDGE,"E6.bottom");var subQ1=sQuery(id+"F0.wireOp",EDGE,"E1.0");Q23=makeQuery(id+"F3.opExtrude","SWEPT_EDGE",EDGE,{"disambiguationData":[OSD([subQ1,subQ0]),TDD([makeQuery(id+"F0.imprint","INTERSECT",VERTEX,{"disambiguationData":[OD(0.0)],"derivedFrom":[subQ1,subQ0]})])]});}
            var Q24;
            {var subQ0=sQuery(id+"F0.wireOp",EDGE,"E1.0");var subQ3=sQuery(id+"F0.wireOp",EDGE,"E6.top");var subQ22=sQuery(id+"F1.wireOp",EDGE,"E12");Q24=makeQuery(id+"F7.boolean.opBoolean","INTERSECT",EDGE,{"disambiguationData":[OD(0.0)],"derivedFrom":[makeQuery(id+"F5.boolean.opBoolean","MERGE",FACE,{"derivedFrom":[makeQuery(id+"F3.boolean.opBoolean","SPLIT",FACE,{"disambiguationData":[TD([makeQuery(id+"F3.opExtrude","SWEPT_FACE",FACE,{"disambiguationData":[OSD([subQ3])]})])],"derivedFrom":makeQuery(id+"F2.opExtrude","SWEPT_FACE",FACE,{"disambiguationData":[OSD([subQ22])]})}),makeQuery(id+"F5.opExtrude","SWEPT_FACE",FACE,{"disambiguationData":[OSD([subQ0]),TDD([makeQuery(id+"F0.imprint","IMPRINT",EDGE,{"disambiguationData":[TD([[makeQuery(id+"F0.imprint","INTERSECT",VERTEX,{"disambiguationData":[OD(0.0)],"derivedFrom":[subQ0,subQ3]}),-1.0]])],"derivedFrom":subQ0})])]}),makeQuery(id+"F5.opExtrude","SWEPT_FACE",FACE,{"disambiguationData":[OSD([subQ0]),TDD([makeQuery(id+"F0.imprint","IMPRINT",EDGE,{"disambiguationData":[TD([[makeQuery(id+"F0.imprint","INTERSECT",VERTEX,{"disambiguationData":[OD(1.0)],"derivedFrom":[subQ0,sQuery(id+"F0.wireOp",EDGE,"E8.right")]}),-1.0]])],"derivedFrom":subQ0})])]}),makeQuery(id+"F5.opExtrude","SWEPT_FACE",FACE,{"disambiguationData":[OSD([subQ0]),TDD([makeQuery(id+"F0.imprint","IMPRINT",EDGE,{"disambiguationData":[TD([[makeQuery(id+"F0.imprint","INTERSECT",VERTEX,{"disambiguationData":[OD(1.0)],"derivedFrom":[subQ0,sQuery(id+"F0.wireOp",EDGE,"E9.right")]}),-1.0]])],"derivedFrom":subQ0})])]})]}),makeQuery(id+"F7.opExtrude","SWEPT_FACE",FACE,{"disambiguationData":[OSD([sQuery(id+"F6.wireOp",EDGE,"E28")])]})]});}
            var Q25;
            {var subQ0=sQuery(id+"F0.wireOp",EDGE,"E8.right");Q25=makeQuery(id+"F7.boolean.opBoolean","INTERSECT",EDGE,{"derivedFrom":[makeQuery(id+"F5.boolean.opBoolean","COPY",FACE,{"derivedFrom":makeQuery(id+"F5.opExtrude","SWEPT_FACE",FACE,{"disambiguationData":[OSD([subQ0]),TDD([makeQuery(id+"F0.imprint","IMPRINT",EDGE,{"disambiguationData":[TD([[makeQuery(id+"F0.imprint","INTERSECT",VERTEX,{"disambiguationData":[OD(1.0)],"derivedFrom":[sQuery(id+"F0.wireOp",EDGE,"E1.0"),subQ0]}),1.0]])],"derivedFrom":subQ0})])]})}),makeQuery(id+"F7.opExtrude","SWEPT_FACE",FACE,{"disambiguationData":[OSD([sQuery(id+"F6.wireOp",EDGE,"E28")])]})]});}
            var Q26;
            {var subQ0=sQuery(id+"F0.wireOp",EDGE,"E9.right");var subQ1=sQuery(id+"F0.wireOp",EDGE,"E1.0");Q26=makeQuery(id+"F5.boolean.opBoolean","COPY",EDGE,{"derivedFrom":makeQuery(id+"F5.opExtrude","SWEPT_EDGE",EDGE,{"disambiguationData":[OSD([subQ1,subQ0]),TDD([makeQuery(id+"F0.imprint","INTERSECT",VERTEX,{"disambiguationData":[OD(1.0)],"derivedFrom":[subQ1,subQ0]})])]})});}
            var Q27;
            {var subQ1=sQuery(id+"F0.wireOp",EDGE,"E9.left");var subQ5=sQuery(id+"F0.wireOp",EDGE,"E6.top");var subQ6=sQuery(id+"F1.wireOp",EDGE,"E11");var subQ7=makeQuery(id+"F4.opExtrude","CAP_FACE",FACE,{"disambiguationData":[OSD([subQ6])],"isStart":false});var subQ8=sQuery(id+"F1.wireOp",EDGE,"E12");var subQ9=makeQuery(id+"F2.opExtrude","SWEPT_FACE",FACE,{"disambiguationData":[OSD([subQ8])]});Q27=makeQuery(id+"F5.boolean.opBoolean","SPLIT",EDGE,{"disambiguationData":[TD([makeQuery(id+"F5.opExtrude","SWEPT_FACE",FACE,{"disambiguationData":[OSD([subQ1])]})])],"derivedFrom":makeQuery(id+"F4.boolean.opBoolean","INTERSECT",EDGE,{"derivedFrom":[makeQuery(id+"F3.boolean.opBoolean","SPLIT",FACE,{"disambiguationData":[TD([makeQuery(id+"F3.opExtrude","SWEPT_FACE",FACE,{"disambiguationData":[OSD([subQ5])]})])],"derivedFrom":subQ9}),subQ7]})});}
            var Q28;
            {var subQ0=sQuery(id+"F0.wireOp",EDGE,"E7.bottom");Q28=makeQuery(id+"F7.boolean.opBoolean","INTERSECT",EDGE,{"derivedFrom":[makeQuery(id+"F5.boolean.opBoolean","MERGE",FACE,{"derivedFrom":[makeQuery(id+"F3.opExtrude","SWEPT_FACE",FACE,{"disambiguationData":[OSD([subQ0]),TDD([makeQuery(id+"F0.imprint","IMPRINT",EDGE,{"disambiguationData":[TD([[makeQuery(id+"F0.imprint","INTERSECT",VERTEX,{"disambiguationData":[OD(1.0)],"derivedFrom":[sQuery(id+"F0.wireOp",EDGE,"E1.0"),subQ0]}),1.0]])],"derivedFrom":subQ0})])]}),makeQuery(id+"F5.opExtrude","SWEPT_FACE",FACE,{"disambiguationData":[OSD([subQ0])]})]}),makeQuery(id+"F7.opExtrude","SWEPT_FACE",FACE,{"disambiguationData":[OSD([sQuery(id+"F6.wireOp",EDGE,"E27")])]})]});}
            var Q29;
            {var subQ0=sQuery(id+"F0.wireOp",EDGE,"E1.0");var subQ3=sQuery(id+"F0.wireOp",EDGE,"E6.top");var subQ22=sQuery(id+"F1.wireOp",EDGE,"E12");Q29=makeQuery(id+"F7.boolean.opBoolean","INTERSECT",EDGE,{"disambiguationData":[OD(0.0)],"derivedFrom":[makeQuery(id+"F5.boolean.opBoolean","MERGE",FACE,{"derivedFrom":[makeQuery(id+"F3.boolean.opBoolean","SPLIT",FACE,{"disambiguationData":[TD([makeQuery(id+"F3.opExtrude","SWEPT_FACE",FACE,{"disambiguationData":[OSD([subQ3])]})])],"derivedFrom":makeQuery(id+"F2.opExtrude","SWEPT_FACE",FACE,{"disambiguationData":[OSD([subQ22])]})}),makeQuery(id+"F5.opExtrude","SWEPT_FACE",FACE,{"disambiguationData":[OSD([subQ0]),TDD([makeQuery(id+"F0.imprint","IMPRINT",EDGE,{"disambiguationData":[TD([[makeQuery(id+"F0.imprint","INTERSECT",VERTEX,{"disambiguationData":[OD(0.0)],"derivedFrom":[subQ0,subQ3]}),-1.0]])],"derivedFrom":subQ0})])]}),makeQuery(id+"F5.opExtrude","SWEPT_FACE",FACE,{"disambiguationData":[OSD([subQ0]),TDD([makeQuery(id+"F0.imprint","IMPRINT",EDGE,{"disambiguationData":[TD([[makeQuery(id+"F0.imprint","INTERSECT",VERTEX,{"disambiguationData":[OD(1.0)],"derivedFrom":[subQ0,sQuery(id+"F0.wireOp",EDGE,"E8.right")]}),-1.0]])],"derivedFrom":subQ0})])]}),makeQuery(id+"F5.opExtrude","SWEPT_FACE",FACE,{"disambiguationData":[OSD([subQ0]),TDD([makeQuery(id+"F0.imprint","IMPRINT",EDGE,{"disambiguationData":[TD([[makeQuery(id+"F0.imprint","INTERSECT",VERTEX,{"disambiguationData":[OD(1.0)],"derivedFrom":[subQ0,sQuery(id+"F0.wireOp",EDGE,"E9.right")]}),-1.0]])],"derivedFrom":subQ0})])]})]}),makeQuery(id+"F7.opExtrude","SWEPT_FACE",FACE,{"disambiguationData":[OSD([sQuery(id+"F6.wireOp",EDGE,"E29")])]})]});}
            var Q30;
            Q30=makeQuery(id+"F7.boolean.opBoolean","INTERSECT",EDGE,{"derivedFrom":[makeQuery(id+"F5.boolean.opBoolean","COPY",FACE,{"derivedFrom":makeQuery(id+"F5.opExtrude","SWEPT_FACE",FACE,{"disambiguationData":[OSD([sQuery(id+"F0.wireOp",EDGE,"E3.left")])]})}),makeQuery(id+"F7.opExtrude","SWEPT_FACE",FACE,{"disambiguationData":[OSD([sQuery(id+"F6.wireOp",EDGE,"E29")])]})]});
            var Q31;
            {var subQ0=sQuery(id+"F0.wireOp",EDGE,"E1.0");var subQ3=sQuery(id+"F0.wireOp",EDGE,"E6.top");var subQ22=sQuery(id+"F1.wireOp",EDGE,"E12");Q31=makeQuery(id+"F7.boolean.opBoolean","INTERSECT",EDGE,{"disambiguationData":[OD(1.0)],"derivedFrom":[makeQuery(id+"F5.boolean.opBoolean","MERGE",FACE,{"derivedFrom":[makeQuery(id+"F3.boolean.opBoolean","SPLIT",FACE,{"disambiguationData":[TD([makeQuery(id+"F3.opExtrude","SWEPT_FACE",FACE,{"disambiguationData":[OSD([subQ3])]})])],"derivedFrom":makeQuery(id+"F2.opExtrude","SWEPT_FACE",FACE,{"disambiguationData":[OSD([subQ22])]})}),makeQuery(id+"F5.opExtrude","SWEPT_FACE",FACE,{"disambiguationData":[OSD([subQ0]),TDD([makeQuery(id+"F0.imprint","IMPRINT",EDGE,{"disambiguationData":[TD([[makeQuery(id+"F0.imprint","INTERSECT",VERTEX,{"disambiguationData":[OD(0.0)],"derivedFrom":[subQ0,subQ3]}),-1.0]])],"derivedFrom":subQ0})])]}),makeQuery(id+"F5.opExtrude","SWEPT_FACE",FACE,{"disambiguationData":[OSD([subQ0]),TDD([makeQuery(id+"F0.imprint","IMPRINT",EDGE,{"disambiguationData":[TD([[makeQuery(id+"F0.imprint","INTERSECT",VERTEX,{"disambiguationData":[OD(1.0)],"derivedFrom":[subQ0,sQuery(id+"F0.wireOp",EDGE,"E8.right")]}),-1.0]])],"derivedFrom":subQ0})])]}),makeQuery(id+"F5.opExtrude","SWEPT_FACE",FACE,{"disambiguationData":[OSD([subQ0]),TDD([makeQuery(id+"F0.imprint","IMPRINT",EDGE,{"disambiguationData":[TD([[makeQuery(id+"F0.imprint","INTERSECT",VERTEX,{"disambiguationData":[OD(1.0)],"derivedFrom":[subQ0,sQuery(id+"F0.wireOp",EDGE,"E9.right")]}),-1.0]])],"derivedFrom":subQ0})])]})]}),makeQuery(id+"F7.opExtrude","SWEPT_FACE",FACE,{"disambiguationData":[OSD([sQuery(id+"F6.wireOp",EDGE,"E29")])]})]});}
            var Q32;
            {var subQ0=sQuery(id+"F0.wireOp",EDGE,"E1.0");var subQ3=sQuery(id+"F0.wireOp",EDGE,"E6.top");var subQ22=sQuery(id+"F1.wireOp",EDGE,"E12");Q32=makeQuery(id+"F7.boolean.opBoolean","INTERSECT",EDGE,{"disambiguationData":[OD(1.0)],"derivedFrom":[makeQuery(id+"F5.boolean.opBoolean","MERGE",FACE,{"derivedFrom":[makeQuery(id+"F3.boolean.opBoolean","SPLIT",FACE,{"disambiguationData":[TD([makeQuery(id+"F3.opExtrude","SWEPT_FACE",FACE,{"disambiguationData":[OSD([subQ3])]})])],"derivedFrom":makeQuery(id+"F2.opExtrude","SWEPT_FACE",FACE,{"disambiguationData":[OSD([subQ22])]})}),makeQuery(id+"F5.opExtrude","SWEPT_FACE",FACE,{"disambiguationData":[OSD([subQ0]),TDD([makeQuery(id+"F0.imprint","IMPRINT",EDGE,{"disambiguationData":[TD([[makeQuery(id+"F0.imprint","INTERSECT",VERTEX,{"disambiguationData":[OD(0.0)],"derivedFrom":[subQ0,subQ3]}),-1.0]])],"derivedFrom":subQ0})])]}),makeQuery(id+"F5.opExtrude","SWEPT_FACE",FACE,{"disambiguationData":[OSD([subQ0]),TDD([makeQuery(id+"F0.imprint","IMPRINT",EDGE,{"disambiguationData":[TD([[makeQuery(id+"F0.imprint","INTERSECT",VERTEX,{"disambiguationData":[OD(1.0)],"derivedFrom":[subQ0,sQuery(id+"F0.wireOp",EDGE,"E8.right")]}),-1.0]])],"derivedFrom":subQ0})])]}),makeQuery(id+"F5.opExtrude","SWEPT_FACE",FACE,{"disambiguationData":[OSD([subQ0]),TDD([makeQuery(id+"F0.imprint","IMPRINT",EDGE,{"disambiguationData":[TD([[makeQuery(id+"F0.imprint","INTERSECT",VERTEX,{"disambiguationData":[OD(1.0)],"derivedFrom":[subQ0,sQuery(id+"F0.wireOp",EDGE,"E9.right")]}),-1.0]])],"derivedFrom":subQ0})])]})]}),makeQuery(id+"F7.opExtrude","SWEPT_FACE",FACE,{"disambiguationData":[OSD([sQuery(id+"F6.wireOp",EDGE,"E28")])]})]});}
            var Q33;
            Q33=makeQuery(id+"F5.boolean.opBoolean","COPY",EDGE,{"derivedFrom":makeQuery(id+"F5.opExtrude","SWEPT_EDGE",EDGE,{"disambiguationData":[OSD([sQuery(id+"F0.wireOp",EDGE,"E1.0"),sQuery(id+"F0.wireOp",EDGE,"E9.left")])]})});
            var Q34;
            {var subQ0=sQuery(id+"F0.wireOp",EDGE,"E7.top");var subQ1=makeQuery(id+"F0.imprint","IMPRINT",EDGE,{"disambiguationData":[TD([[makeQuery(id+"F0.imprint","INTERSECT",VERTEX,{"disambiguationData":[OD(1.0)],"derivedFrom":[sQuery(id+"F0.wireOp",EDGE,"E1.0"),subQ0]}),1.0]])],"derivedFrom":subQ0});Q34=makeQuery(id+"F7.boolean.opBoolean","INTERSECT",EDGE,{"derivedFrom":[makeQuery(id+"F5.boolean.opBoolean","MERGE",FACE,{"derivedFrom":[makeQuery(id+"F3.opExtrude","SWEPT_FACE",FACE,{"disambiguationData":[OSD([subQ0]),TDD([subQ1])]}),makeQuery(id+"F5.opExtrude","SWEPT_FACE",FACE,{"disambiguationData":[OSD([subQ0]),TDD([subQ1])]})]}),makeQuery(id+"F7.opExtrude","SWEPT_FACE",FACE,{"disambiguationData":[OSD([sQuery(id+"F6.wireOp",EDGE,"E27")])]})]});}
            var Q35;
            {var subQ0=sQuery(id+"F0.wireOp",EDGE,"E1.0");var subQ3=sQuery(id+"F0.wireOp",EDGE,"E6.top");var subQ22=sQuery(id+"F1.wireOp",EDGE,"E12");Q35=makeQuery(id+"F7.boolean.opBoolean","INTERSECT",EDGE,{"derivedFrom":[makeQuery(id+"F5.boolean.opBoolean","MERGE",FACE,{"derivedFrom":[makeQuery(id+"F3.boolean.opBoolean","SPLIT",FACE,{"disambiguationData":[TD([makeQuery(id+"F3.opExtrude","SWEPT_FACE",FACE,{"disambiguationData":[OSD([subQ3])]})])],"derivedFrom":makeQuery(id+"F2.opExtrude","SWEPT_FACE",FACE,{"disambiguationData":[OSD([subQ22])]})}),makeQuery(id+"F5.opExtrude","SWEPT_FACE",FACE,{"disambiguationData":[OSD([subQ0]),TDD([makeQuery(id+"F0.imprint","IMPRINT",EDGE,{"disambiguationData":[TD([[makeQuery(id+"F0.imprint","INTERSECT",VERTEX,{"disambiguationData":[OD(0.0)],"derivedFrom":[subQ0,subQ3]}),-1.0]])],"derivedFrom":subQ0})])]}),makeQuery(id+"F5.opExtrude","SWEPT_FACE",FACE,{"disambiguationData":[OSD([subQ0]),TDD([makeQuery(id+"F0.imprint","IMPRINT",EDGE,{"disambiguationData":[TD([[makeQuery(id+"F0.imprint","INTERSECT",VERTEX,{"disambiguationData":[OD(1.0)],"derivedFrom":[subQ0,sQuery(id+"F0.wireOp",EDGE,"E8.right")]}),-1.0]])],"derivedFrom":subQ0})])]}),makeQuery(id+"F5.opExtrude","SWEPT_FACE",FACE,{"disambiguationData":[OSD([subQ0]),TDD([makeQuery(id+"F0.imprint","IMPRINT",EDGE,{"disambiguationData":[TD([[makeQuery(id+"F0.imprint","INTERSECT",VERTEX,{"disambiguationData":[OD(1.0)],"derivedFrom":[subQ0,sQuery(id+"F0.wireOp",EDGE,"E9.right")]}),-1.0]])],"derivedFrom":subQ0})])]})]}),makeQuery(id+"F7.opExtrude","SWEPT_FACE",FACE,{"disambiguationData":[OSD([sQuery(id+"F6.wireOp",EDGE,"E27")])]})]});}
            var Q36;
            {var subQ0=sQuery(id+"F0.wireOp",EDGE,"E7.bottom");var subQ1=sQuery(id+"F0.wireOp",EDGE,"E1.0");var subQ2=makeQuery(id+"F0.imprint","INTERSECT",VERTEX,{"disambiguationData":[OD(1.0)],"derivedFrom":[subQ1,subQ0]});var subQ22=sQuery(id+"F1.wireOp",EDGE,"E12");var subQ24=sQuery(id+"F0.wireOp",EDGE,"E2.right");Q36=makeQuery(id+"F7.boolean.opBoolean","INTERSECT",EDGE,{"disambiguationData":[OD(0.0)],"derivedFrom":[makeQuery(id+"F5.boolean.opBoolean","MERGE",FACE,{"derivedFrom":[makeQuery(id+"F3.boolean.opBoolean","SPLIT",FACE,{"disambiguationData":[TD([makeQuery(id+"F3.opExtrude","SWEPT_FACE",FACE,{"disambiguationData":[OSD([subQ24])]})])],"derivedFrom":makeQuery(id+"F2.opExtrude","SWEPT_FACE",FACE,{"disambiguationData":[OSD([subQ22])]})}),makeQuery(id+"F5.opExtrude","SWEPT_FACE",FACE,{"disambiguationData":[OSD([subQ1]),TDD([makeQuery(id+"F0.imprint","IMPRINT",EDGE,{"disambiguationData":[TD([[subQ2,-1.0]])],"derivedFrom":subQ1})])]})]}),makeQuery(id+"F7.opExtrude","SWEPT_FACE",FACE,{"disambiguationData":[OSD([sQuery(id+"F6.wireOp",EDGE,"E26")])]})]});}
            var Q37;
            {var subQ0=sQuery(id+"F0.wireOp",EDGE,"E7.bottom");var subQ1=sQuery(id+"F0.wireOp",EDGE,"E1.0");var subQ2=makeQuery(id+"F0.imprint","INTERSECT",VERTEX,{"disambiguationData":[OD(1.0)],"derivedFrom":[subQ1,subQ0]});var subQ22=sQuery(id+"F1.wireOp",EDGE,"E12");var subQ24=sQuery(id+"F0.wireOp",EDGE,"E2.right");Q37=makeQuery(id+"F7.boolean.opBoolean","INTERSECT",EDGE,{"derivedFrom":[makeQuery(id+"F5.boolean.opBoolean","MERGE",FACE,{"derivedFrom":[makeQuery(id+"F3.boolean.opBoolean","SPLIT",FACE,{"disambiguationData":[TD([makeQuery(id+"F3.opExtrude","SWEPT_FACE",FACE,{"disambiguationData":[OSD([subQ24])]})])],"derivedFrom":makeQuery(id+"F2.opExtrude","SWEPT_FACE",FACE,{"disambiguationData":[OSD([subQ22])]})}),makeQuery(id+"F5.opExtrude","SWEPT_FACE",FACE,{"disambiguationData":[OSD([subQ1]),TDD([makeQuery(id+"F0.imprint","IMPRINT",EDGE,{"disambiguationData":[TD([[subQ2,-1.0]])],"derivedFrom":subQ1})])]})]}),makeQuery(id+"F7.opExtrude","SWEPT_FACE",FACE,{"disambiguationData":[OSD([sQuery(id+"F6.wireOp",EDGE,"E27")])]})]});}
            var Q38;
            {var subQ0=sQuery(id+"F0.wireOp",EDGE,"E7.bottom");var subQ1=sQuery(id+"F0.wireOp",EDGE,"E1.0");var subQ2=makeQuery(id+"F0.imprint","INTERSECT",VERTEX,{"disambiguationData":[OD(1.0)],"derivedFrom":[subQ1,subQ0]});var subQ22=sQuery(id+"F1.wireOp",EDGE,"E12");var subQ24=sQuery(id+"F0.wireOp",EDGE,"E2.right");Q38=makeQuery(id+"F7.boolean.opBoolean","INTERSECT",EDGE,{"disambiguationData":[OD(1.0)],"derivedFrom":[makeQuery(id+"F5.boolean.opBoolean","MERGE",FACE,{"derivedFrom":[makeQuery(id+"F3.boolean.opBoolean","SPLIT",FACE,{"disambiguationData":[TD([makeQuery(id+"F3.opExtrude","SWEPT_FACE",FACE,{"disambiguationData":[OSD([subQ24])]})])],"derivedFrom":makeQuery(id+"F2.opExtrude","SWEPT_FACE",FACE,{"disambiguationData":[OSD([subQ22])]})}),makeQuery(id+"F5.opExtrude","SWEPT_FACE",FACE,{"disambiguationData":[OSD([subQ1]),TDD([makeQuery(id+"F0.imprint","IMPRINT",EDGE,{"disambiguationData":[TD([[subQ2,-1.0]])],"derivedFrom":subQ1})])]})]}),makeQuery(id+"F7.opExtrude","SWEPT_FACE",FACE,{"disambiguationData":[OSD([sQuery(id+"F6.wireOp",EDGE,"E26")])]})]});}
            var Q39;
            {var subQ0=sQuery(id+"F0.wireOp",EDGE,"E1.0");var subQ1=sQuery(id+"F0.wireOp",EDGE,"E2.left");var subQ23=sQuery(id+"F1.wireOp",EDGE,"E12");Q39=makeQuery(id+"F7.boolean.opBoolean","INTERSECT",EDGE,{"disambiguationData":[OD(1.0)],"derivedFrom":[makeQuery(id+"F5.boolean.opBoolean","MERGE",FACE,{"derivedFrom":[makeQuery(id+"F3.boolean.opBoolean","SPLIT",FACE,{"disambiguationData":[TD([makeQuery(id+"F3.opExtrude","SWEPT_FACE",FACE,{"disambiguationData":[OSD([subQ1])]})])],"derivedFrom":makeQuery(id+"F2.opExtrude","SWEPT_FACE",FACE,{"disambiguationData":[OSD([subQ23])]})}),makeQuery(id+"F5.opExtrude","SWEPT_FACE",FACE,{"disambiguationData":[OSD([subQ0]),TDD([makeQuery(id+"F0.imprint","IMPRINT",EDGE,{"disambiguationData":[TD([[makeQuery(id+"F0.imprint","INTERSECT",VERTEX,{"disambiguationData":[OD(0.0)],"derivedFrom":[subQ0,subQ1]}),-1.0]])],"derivedFrom":subQ0})])]}),makeQuery(id+"F5.opExtrude","SWEPT_FACE",FACE,{"disambiguationData":[OSD([subQ0]),TDD([makeQuery(id+"F0.imprint","IMPRINT",EDGE,{"disambiguationData":[TD([[makeQuery(id+"F0.imprint","INTERSECT",VERTEX,{"disambiguationData":[OD(0.0)],"derivedFrom":[subQ0,sQuery(id+"F0.wireOp",EDGE,"E8.left")]}),-1.0]])],"derivedFrom":subQ0})])]})]}),makeQuery(id+"F7.opExtrude","SWEPT_FACE",FACE,{"disambiguationData":[OSD([sQuery(id+"F6.wireOp",EDGE,"E25")])]})]});}
            var Q40;
            Q40=makeQuery(id+"F7.boolean.opBoolean","INTERSECT",EDGE,{"derivedFrom":[makeQuery(id+"F5.boolean.opBoolean","COPY",FACE,{"derivedFrom":makeQuery(id+"F5.opExtrude","SWEPT_FACE",FACE,{"disambiguationData":[OSD([sQuery(id+"F0.wireOp",EDGE,"E8.left")])]})}),makeQuery(id+"F7.opExtrude","SWEPT_FACE",FACE,{"disambiguationData":[OSD([sQuery(id+"F6.wireOp",EDGE,"E25")])]})]});
            var Q41;
            Q41=makeQuery(id+"F7.boolean.opBoolean","INTERSECT",EDGE,{"derivedFrom":[makeQuery(id+"F4.opExtrude","CAP_FACE",FACE,{"disambiguationData":[OSD([sQuery(id+"F1.wireOp",EDGE,"E11")])],"isStart":false}),makeQuery(id+"F7.opExtrude","SWEPT_FACE",FACE,{"disambiguationData":[OSD([sQuery(id+"F6.wireOp",EDGE,"E25")])]})]});
            var Q42;
            {var subQ0=sQuery(id+"F0.wireOp",EDGE,"E1.0");var subQ1=sQuery(id+"F0.wireOp",EDGE,"E2.left");var subQ23=sQuery(id+"F1.wireOp",EDGE,"E12");Q42=makeQuery(id+"F7.boolean.opBoolean","INTERSECT",EDGE,{"disambiguationData":[OD(0.0)],"derivedFrom":[makeQuery(id+"F5.boolean.opBoolean","MERGE",FACE,{"derivedFrom":[makeQuery(id+"F3.boolean.opBoolean","SPLIT",FACE,{"disambiguationData":[TD([makeQuery(id+"F3.opExtrude","SWEPT_FACE",FACE,{"disambiguationData":[OSD([subQ1])]})])],"derivedFrom":makeQuery(id+"F2.opExtrude","SWEPT_FACE",FACE,{"disambiguationData":[OSD([subQ23])]})}),makeQuery(id+"F5.opExtrude","SWEPT_FACE",FACE,{"disambiguationData":[OSD([subQ0]),TDD([makeQuery(id+"F0.imprint","IMPRINT",EDGE,{"disambiguationData":[TD([[makeQuery(id+"F0.imprint","INTERSECT",VERTEX,{"disambiguationData":[OD(0.0)],"derivedFrom":[subQ0,subQ1]}),-1.0]])],"derivedFrom":subQ0})])]}),makeQuery(id+"F5.opExtrude","SWEPT_FACE",FACE,{"disambiguationData":[OSD([subQ0]),TDD([makeQuery(id+"F0.imprint","IMPRINT",EDGE,{"disambiguationData":[TD([[makeQuery(id+"F0.imprint","INTERSECT",VERTEX,{"disambiguationData":[OD(0.0)],"derivedFrom":[subQ0,sQuery(id+"F0.wireOp",EDGE,"E8.left")]}),-1.0]])],"derivedFrom":subQ0})])]})]}),makeQuery(id+"F7.opExtrude","SWEPT_FACE",FACE,{"disambiguationData":[OSD([sQuery(id+"F6.wireOp",EDGE,"E25")])]})]});}
            var Q43;
            {var subQ0=sQuery(id+"F0.wireOp",EDGE,"E7.top");var subQ1=makeQuery(id+"F0.imprint","IMPRINT",EDGE,{"disambiguationData":[TD([[makeQuery(id+"F0.imprint","INTERSECT",VERTEX,{"disambiguationData":[OD(0.0)],"derivedFrom":[sQuery(id+"F0.wireOp",EDGE,"E1.0"),subQ0]}),-1.0]])],"derivedFrom":subQ0});Q43=makeQuery(id+"F7.boolean.opBoolean","INTERSECT",EDGE,{"derivedFrom":[makeQuery(id+"F5.boolean.opBoolean","MERGE",FACE,{"derivedFrom":[makeQuery(id+"F3.opExtrude","SWEPT_FACE",FACE,{"disambiguationData":[OSD([subQ0]),TDD([subQ1])]}),makeQuery(id+"F5.opExtrude","SWEPT_FACE",FACE,{"disambiguationData":[OSD([subQ0]),TDD([subQ1])]})]}),makeQuery(id+"F7.opExtrude","SWEPT_FACE",FACE,{"disambiguationData":[OSD([sQuery(id+"F6.wireOp",EDGE,"E30")])]})]});}
            var Q44;
            {var subQ0=sQuery(id+"F0.wireOp",EDGE,"E7.top");var subQ1=sQuery(id+"F0.wireOp",EDGE,"E1.0");var subQ2=makeQuery(id+"F0.imprint","INTERSECT",VERTEX,{"disambiguationData":[OD(0.0)],"derivedFrom":[subQ1,subQ0]});var subQ3=sQuery(id+"F0.wireOp",EDGE,"E6.bottom");var subQ22=sQuery(id+"F1.wireOp",EDGE,"E12");Q44=makeQuery(id+"F7.boolean.opBoolean","INTERSECT",EDGE,{"derivedFrom":[makeQuery(id+"F5.boolean.opBoolean","MERGE",FACE,{"derivedFrom":[makeQuery(id+"F3.boolean.opBoolean","SPLIT",FACE,{"disambiguationData":[TD([makeQuery(id+"F3.opExtrude","SWEPT_FACE",FACE,{"disambiguationData":[OSD([subQ3])]})])],"derivedFrom":makeQuery(id+"F2.opExtrude","SWEPT_FACE",FACE,{"disambiguationData":[OSD([subQ22])]})}),makeQuery(id+"F5.opExtrude","SWEPT_FACE",FACE,{"disambiguationData":[OSD([subQ1]),TDD([makeQuery(id+"F0.imprint","IMPRINT",EDGE,{"disambiguationData":[TD([[subQ2,-1.0]])],"derivedFrom":subQ1})])]})]}),makeQuery(id+"F7.opExtrude","SWEPT_FACE",FACE,{"disambiguationData":[OSD([sQuery(id+"F6.wireOp",EDGE,"E30")])]})]});}
            var Q45;
            {var subQ0=sQuery(id+"F0.wireOp",EDGE,"E7.bottom");Q45=makeQuery(id+"F7.boolean.opBoolean","INTERSECT",EDGE,{"derivedFrom":[makeQuery(id+"F3.opExtrude","SWEPT_FACE",FACE,{"disambiguationData":[OSD([subQ0]),TDD([makeQuery(id+"F0.imprint","IMPRINT",EDGE,{"disambiguationData":[TD([[makeQuery(id+"F0.imprint","INTERSECT",VERTEX,{"disambiguationData":[OD(0.0)],"derivedFrom":[sQuery(id+"F0.wireOp",EDGE,"E1.0"),subQ0]}),-1.0]])],"derivedFrom":subQ0})])]}),makeQuery(id+"F7.opExtrude","SWEPT_FACE",FACE,{"disambiguationData":[OSD([sQuery(id+"F6.wireOp",EDGE,"E30")])]})]});}
            var Q46;
            {var subQ0=sQuery(id+"F0.wireOp",EDGE,"E1.0");var subQ1=sQuery(id+"F0.wireOp",EDGE,"E2.left");var subQ23=sQuery(id+"F1.wireOp",EDGE,"E12");Q46=makeQuery(id+"F7.boolean.opBoolean","INTERSECT",EDGE,{"derivedFrom":[makeQuery(id+"F5.boolean.opBoolean","MERGE",FACE,{"derivedFrom":[makeQuery(id+"F3.boolean.opBoolean","SPLIT",FACE,{"disambiguationData":[TD([makeQuery(id+"F3.opExtrude","SWEPT_FACE",FACE,{"disambiguationData":[OSD([subQ1])]})])],"derivedFrom":makeQuery(id+"F2.opExtrude","SWEPT_FACE",FACE,{"disambiguationData":[OSD([subQ23])]})}),makeQuery(id+"F5.opExtrude","SWEPT_FACE",FACE,{"disambiguationData":[OSD([subQ0]),TDD([makeQuery(id+"F0.imprint","IMPRINT",EDGE,{"disambiguationData":[TD([[makeQuery(id+"F0.imprint","INTERSECT",VERTEX,{"disambiguationData":[OD(0.0)],"derivedFrom":[subQ0,subQ1]}),-1.0]])],"derivedFrom":subQ0})])]}),makeQuery(id+"F5.opExtrude","SWEPT_FACE",FACE,{"disambiguationData":[OSD([subQ0]),TDD([makeQuery(id+"F0.imprint","IMPRINT",EDGE,{"disambiguationData":[TD([[makeQuery(id+"F0.imprint","INTERSECT",VERTEX,{"disambiguationData":[OD(0.0)],"derivedFrom":[subQ0,sQuery(id+"F0.wireOp",EDGE,"E8.left")]}),-1.0]])],"derivedFrom":subQ0})])]})]}),makeQuery(id+"F7.opExtrude","SWEPT_FACE",FACE,{"disambiguationData":[OSD([sQuery(id+"F6.wireOp",EDGE,"E30")])]})]});}
            var Q47;
            {var subQ0=sQuery(id+"F0.wireOp",EDGE,"E9.right");var subQ1=sQuery(id+"F0.wireOp",EDGE,"E1.0");Q47=makeQuery(id+"F5.boolean.opBoolean","COPY",EDGE,{"derivedFrom":makeQuery(id+"F5.opExtrude","SWEPT_EDGE",EDGE,{"disambiguationData":[OSD([subQ1,subQ0]),TDD([makeQuery(id+"F0.imprint","INTERSECT",VERTEX,{"disambiguationData":[OD(0.0)],"derivedFrom":[subQ1,subQ0]})])]})});}
            var Q48;
            {var subQ0=sQuery(id+"F0.wireOp",EDGE,"E6.top");var subQ1=sQuery(id+"F0.wireOp",EDGE,"E1.0");Q48=makeQuery(id+"F5.boolean.opBoolean","COPY",EDGE,{"derivedFrom":makeQuery(id+"F5.opExtrude","SWEPT_EDGE",EDGE,{"disambiguationData":[OSD([subQ1,subQ0]),TDD([makeQuery(id+"F0.imprint","INTERSECT",VERTEX,{"disambiguationData":[OD(1.0)],"derivedFrom":[subQ1,subQ0]})])]})});}
            fillet(context, id + "F8", {"entities" : qUnion([Q0, Q1, Q2, Q3, Q4, Q5, Q6, Q7, Q8, Q9, Q10, Q11, Q12, Q13, Q14, Q15, Q16, Q17, Q18, Q19, Q20, Q21, Q22, Q23, Q24, Q25, Q26, Q27, Q28, Q29, Q30, Q31, Q32, Q33, Q34, Q35, Q36, Q37, Q38, Q39, Q40, Q41, Q42, Q43, Q44, Q45, Q46, Q47, Q48]), "radius" : 1 * mm, "tangentPropagation" : true, "allowEdgeOverflow" : false});
        }
        {
            var Q0;
            {var subQ0=sQuery(id+"F6.wireOp",EDGE,"E31");var subQ1=sQuery(id+"F6.wireOp",EDGE,"E13");var subQ2=makeQuery(id+"F6.imprint","INTERSECT",VERTEX,{"disambiguationData":[OD(0.0)],"derivedFrom":[subQ1,subQ0]});Q0=makeQuery(id+"F6.imprint","IMPRINT",FACE,{"disambiguationData":[TD([[makeQuery(id+"F6.imprint","IMPRINT",EDGE,{"disambiguationData":[TD([[subQ2,-1.0]])],"derivedFrom":subQ1}),-1.0]])]});}
            var Q1;
            {var subQ0=sQuery(id+"F6.wireOp",EDGE,"E31");var subQ1=sQuery(id+"F6.wireOp",EDGE,"E13");var subQ2=makeQuery(id+"F6.imprint","INTERSECT",VERTEX,{"disambiguationData":[OD(0.0)],"derivedFrom":[subQ1,subQ0]});Q1=makeQuery(id+"F6.imprint","IMPRINT",FACE,{"disambiguationData":[TD([[makeQuery(id+"F6.imprint","IMPRINT",EDGE,{"disambiguationData":[TD([[subQ2,-1.0]])],"derivedFrom":subQ1}),1.0]])]});}
            var Q2;
            {var subQ0=sQuery(id+"F6.wireOp",EDGE,"E32");var subQ1=sQuery(id+"F6.wireOp",EDGE,"E13");var subQ2=makeQuery(id+"F6.imprint","INTERSECT",VERTEX,{"disambiguationData":[OD(0.0)],"derivedFrom":[subQ1,subQ0]});Q2=makeQuery(id+"F6.imprint","IMPRINT",FACE,{"disambiguationData":[TD([[makeQuery(id+"F6.imprint","IMPRINT",EDGE,{"disambiguationData":[TD([[subQ2,-1.0]])],"derivedFrom":subQ1}),-1.0]])]});}
            var Q3;
            {var subQ0=sQuery(id+"F6.wireOp",EDGE,"E32");var subQ1=sQuery(id+"F6.wireOp",EDGE,"E13");var subQ2=makeQuery(id+"F6.imprint","INTERSECT",VERTEX,{"disambiguationData":[OD(0.0)],"derivedFrom":[subQ1,subQ0]});Q3=makeQuery(id+"F6.imprint","IMPRINT",FACE,{"disambiguationData":[TD([[makeQuery(id+"F6.imprint","IMPRINT",EDGE,{"disambiguationData":[TD([[subQ2,-1.0]])],"derivedFrom":subQ1}),1.0]])]});}
            var Q4;
            {var subQ0=sQuery(id+"F6.wireOp",EDGE,"E33");var subQ1=sQuery(id+"F6.wireOp",EDGE,"E13");var subQ2=makeQuery(id+"F6.imprint","INTERSECT",VERTEX,{"disambiguationData":[OD(0.0)],"derivedFrom":[subQ1,subQ0]});Q4=makeQuery(id+"F6.imprint","IMPRINT",FACE,{"disambiguationData":[TD([[makeQuery(id+"F6.imprint","IMPRINT",EDGE,{"disambiguationData":[TD([[subQ2,-1.0]])],"derivedFrom":subQ1}),1.0]])]});}
            var Q5;
            {var subQ0=sQuery(id+"F6.wireOp",EDGE,"E33");var subQ1=sQuery(id+"F6.wireOp",EDGE,"E13");var subQ2=makeQuery(id+"F6.imprint","INTERSECT",VERTEX,{"disambiguationData":[OD(0.0)],"derivedFrom":[subQ1,subQ0]});Q5=makeQuery(id+"F6.imprint","IMPRINT",FACE,{"disambiguationData":[TD([[makeQuery(id+"F6.imprint","IMPRINT",EDGE,{"disambiguationData":[TD([[subQ2,-1.0]])],"derivedFrom":subQ1}),-1.0]])]});}
            var Q6;
            {var subQ0=sQuery(id+"F6.wireOp",EDGE,"E34");var subQ1=sQuery(id+"F6.wireOp",EDGE,"E13");var subQ2=makeQuery(id+"F6.imprint","INTERSECT",VERTEX,{"disambiguationData":[OD(0.0)],"derivedFrom":[subQ1,subQ0]});Q6=makeQuery(id+"F6.imprint","IMPRINT",FACE,{"disambiguationData":[TD([[makeQuery(id+"F6.imprint","IMPRINT",EDGE,{"disambiguationData":[TD([[subQ2,-1.0]])],"derivedFrom":subQ1}),1.0]])]});}
            var Q7;
            {var subQ0=sQuery(id+"F6.wireOp",EDGE,"E34");var subQ1=sQuery(id+"F6.wireOp",EDGE,"E13");var subQ2=makeQuery(id+"F6.imprint","INTERSECT",VERTEX,{"disambiguationData":[OD(0.0)],"derivedFrom":[subQ1,subQ0]});Q7=makeQuery(id+"F6.imprint","IMPRINT",FACE,{"disambiguationData":[TD([[makeQuery(id+"F6.imprint","IMPRINT",EDGE,{"disambiguationData":[TD([[subQ2,-1.0]])],"derivedFrom":subQ1}),-1.0]])]});}
            var Q8;
            {var subQ1=sQuery(id+"F6.wireOp",EDGE,"E36.bottom");Q8=makeQuery(id+"F6.imprint","IMPRINT",FACE,{"disambiguationData":[TD([[makeQuery(id+"F6.imprint","IMPRINT",EDGE,{"derivedFrom":subQ1}),-1.0]])]});}
            var Q9;
            {var subQ0=sQuery(id+"F6.wireOp",EDGE,"E36.top");var subQ1=sQuery(id+"F6.wireOp",EDGE,"E13");var subQ2=makeQuery(id+"F6.imprint","INTERSECT",VERTEX,{"derivedFrom":[subQ1,subQ0]});Q9=makeQuery(id+"F6.imprint","IMPRINT",FACE,{"disambiguationData":[TD([[makeQuery(id+"F6.imprint","IMPRINT",EDGE,{"disambiguationData":[TD([[subQ2,-1.0]])],"derivedFrom":subQ1}),1.0]])]});}
            var Q10;
            {var subQ0=sQuery(id+"F6.wireOp",EDGE,"E35");var subQ1=sQuery(id+"F6.wireOp",EDGE,"E13");var subQ2=makeQuery(id+"F6.imprint","INTERSECT",VERTEX,{"disambiguationData":[OD(0.0)],"derivedFrom":[subQ1,subQ0]});Q10=makeQuery(id+"F6.imprint","IMPRINT",FACE,{"disambiguationData":[TD([[makeQuery(id+"F6.imprint","IMPRINT",EDGE,{"disambiguationData":[TD([[subQ2,-1.0]])],"derivedFrom":subQ1}),-1.0]])]});}
            var Q11;
            {var subQ0=sQuery(id+"F6.wireOp",EDGE,"E35");var subQ1=sQuery(id+"F6.wireOp",EDGE,"E13");var subQ2=makeQuery(id+"F6.imprint","INTERSECT",VERTEX,{"disambiguationData":[OD(0.0)],"derivedFrom":[subQ1,subQ0]});Q11=makeQuery(id+"F6.imprint","IMPRINT",FACE,{"disambiguationData":[TD([[makeQuery(id+"F6.imprint","IMPRINT",EDGE,{"disambiguationData":[TD([[subQ2,-1.0]])],"derivedFrom":subQ1}),1.0]])]});}
            extrude(context, id + "F9", {"entities" : qUnion([Q0, Q1, Q2, Q3, Q4, Q5, Q6, Q7, Q8, Q9, Q10, Q11]), "operationType" : NewBodyOperationType.ADD, "depth" : 11 * mm, "offsetDistance" : 25 * mm, "hasDraft" : true, "draftAngle" : .9 * degree, "draftPullDirection" : true});
        }
        {
            var Q0;
            Q0=makeQuery(id+"F9.opExtrude","CAP_EDGE",EDGE,{"disambiguationData":[OSD([sQuery(id+"F6.wireOp",EDGE,"E35")])],"isStart":false});
            var Q1;
            Q1=makeQuery(id+"F9.opExtrude","CAP_FACE",FACE,{"disambiguationData":[OSD([sQuery(id+"F6.wireOp",EDGE,"E31")])],"isStart":false});
            var Q2;
            Q2=makeQuery(id+"F9.opExtrude","CAP_FACE",FACE,{"disambiguationData":[OSD([sQuery(id+"F6.wireOp",EDGE,"E32")])],"isStart":false});
            var Q3;
            Q3=makeQuery(id+"F9.opExtrude","CAP_FACE",FACE,{"disambiguationData":[OSD([sQuery(id+"F6.wireOp",EDGE,"E33")])],"isStart":false});
            var Q4;
            Q4=makeQuery(id+"F9.opExtrude","CAP_FACE",FACE,{"disambiguationData":[OSD([sQuery(id+"F6.wireOp",EDGE,"E34")])],"isStart":false});
            var Q5;
            Q5=makeQuery(id+"F9.opExtrude","CAP_EDGE",EDGE,{"disambiguationData":[OSD([sQuery(id+"F6.wireOp",EDGE,"E36.left")])],"isStart":false});
            var Q6;
            Q6=makeQuery(id+"F9.opExtrude","CAP_EDGE",EDGE,{"disambiguationData":[OSD([sQuery(id+"F6.wireOp",EDGE,"E36.right")])],"isStart":false});
            var Q7;
            Q7=makeQuery(id+"F9.opExtrude","CAP_EDGE",EDGE,{"disambiguationData":[OSD([sQuery(id+"F6.wireOp",EDGE,"E36.bottom")])],"isStart":false});
            var Q8;
            Q8=makeQuery(id+"F9.opExtrude","CAP_EDGE",EDGE,{"disambiguationData":[OSD([sQuery(id+"F6.wireOp",EDGE,"E36.top")])],"isStart":false});
            fillet(context, id + "F10", {"entities" : qUnion([Q0, Q1, Q2, Q3, Q4, Q5, Q6, Q7, Q8]), "radius" : .45 * mm, "tangentPropagation" : true, "allowEdgeOverflow" : false});
        }
        {
            var Q0;
            {var subQ0=sQuery(id+"F6.wireOp",EDGE,"E35");var subQ1=sQuery(id+"F6.wireOp",EDGE,"E13");var subQ2=makeQuery(id+"F6.imprint","INTERSECT",VERTEX,{"disambiguationData":[OD(0.0)],"derivedFrom":[subQ1,subQ0]});Q0=makeQuery(id+"F6.imprint","IMPRINT",FACE,{"disambiguationData":[TD([[makeQuery(id+"F6.imprint","IMPRINT",EDGE,{"disambiguationData":[TD([[subQ2,-1.0]])],"derivedFrom":subQ1}),-1.0]])]});}
            var Q1;
            {var subQ0=sQuery(id+"F6.wireOp",EDGE,"E35");var subQ1=sQuery(id+"F6.wireOp",EDGE,"E13");var subQ2=makeQuery(id+"F6.imprint","INTERSECT",VERTEX,{"disambiguationData":[OD(0.0)],"derivedFrom":[subQ1,subQ0]});Q1=makeQuery(id+"F6.imprint","IMPRINT",FACE,{"disambiguationData":[TD([[makeQuery(id+"F6.imprint","IMPRINT",EDGE,{"disambiguationData":[TD([[subQ2,-1.0]])],"derivedFrom":subQ1}),1.0]])]});}
            var Q2;
            {var subQ1=sQuery(id+"F6.wireOp",EDGE,"E36.bottom");Q2=makeQuery(id+"F6.imprint","IMPRINT",FACE,{"disambiguationData":[TD([[makeQuery(id+"F6.imprint","IMPRINT",EDGE,{"derivedFrom":subQ1}),-1.0]])]});}
            var Q3;
            {var subQ0=sQuery(id+"F6.wireOp",EDGE,"E36.top");var subQ1=sQuery(id+"F6.wireOp",EDGE,"E13");var subQ2=makeQuery(id+"F6.imprint","INTERSECT",VERTEX,{"derivedFrom":[subQ1,subQ0]});Q3=makeQuery(id+"F6.imprint","IMPRINT",FACE,{"disambiguationData":[TD([[makeQuery(id+"F6.imprint","IMPRINT",EDGE,{"disambiguationData":[TD([[subQ2,-1.0]])],"derivedFrom":subQ1}),1.0]])]});}
            var Q4;
            {var subQ0=sQuery(id+"F6.wireOp",EDGE,"E34");var subQ1=sQuery(id+"F6.wireOp",EDGE,"E13");var subQ2=makeQuery(id+"F6.imprint","INTERSECT",VERTEX,{"disambiguationData":[OD(0.0)],"derivedFrom":[subQ1,subQ0]});Q4=makeQuery(id+"F6.imprint","IMPRINT",FACE,{"disambiguationData":[TD([[makeQuery(id+"F6.imprint","IMPRINT",EDGE,{"disambiguationData":[TD([[subQ2,-1.0]])],"derivedFrom":subQ1}),1.0]])]});}
            var Q5;
            {var subQ0=sQuery(id+"F6.wireOp",EDGE,"E34");var subQ1=sQuery(id+"F6.wireOp",EDGE,"E13");var subQ2=makeQuery(id+"F6.imprint","INTERSECT",VERTEX,{"disambiguationData":[OD(0.0)],"derivedFrom":[subQ1,subQ0]});Q5=makeQuery(id+"F6.imprint","IMPRINT",FACE,{"disambiguationData":[TD([[makeQuery(id+"F6.imprint","IMPRINT",EDGE,{"disambiguationData":[TD([[subQ2,-1.0]])],"derivedFrom":subQ1}),-1.0]])]});}
            var Q6;
            {var subQ0=sQuery(id+"F6.wireOp",EDGE,"E33");var subQ1=sQuery(id+"F6.wireOp",EDGE,"E13");var subQ2=makeQuery(id+"F6.imprint","INTERSECT",VERTEX,{"disambiguationData":[OD(0.0)],"derivedFrom":[subQ1,subQ0]});Q6=makeQuery(id+"F6.imprint","IMPRINT",FACE,{"disambiguationData":[TD([[makeQuery(id+"F6.imprint","IMPRINT",EDGE,{"disambiguationData":[TD([[subQ2,-1.0]])],"derivedFrom":subQ1}),1.0]])]});}
            var Q7;
            {var subQ0=sQuery(id+"F6.wireOp",EDGE,"E33");var subQ1=sQuery(id+"F6.wireOp",EDGE,"E13");var subQ2=makeQuery(id+"F6.imprint","INTERSECT",VERTEX,{"disambiguationData":[OD(0.0)],"derivedFrom":[subQ1,subQ0]});Q7=makeQuery(id+"F6.imprint","IMPRINT",FACE,{"disambiguationData":[TD([[makeQuery(id+"F6.imprint","IMPRINT",EDGE,{"disambiguationData":[TD([[subQ2,-1.0]])],"derivedFrom":subQ1}),-1.0]])]});}
            var Q8;
            {var subQ0=sQuery(id+"F6.wireOp",EDGE,"E32");var subQ1=sQuery(id+"F6.wireOp",EDGE,"E13");var subQ2=makeQuery(id+"F6.imprint","INTERSECT",VERTEX,{"disambiguationData":[OD(0.0)],"derivedFrom":[subQ1,subQ0]});Q8=makeQuery(id+"F6.imprint","IMPRINT",FACE,{"disambiguationData":[TD([[makeQuery(id+"F6.imprint","IMPRINT",EDGE,{"disambiguationData":[TD([[subQ2,-1.0]])],"derivedFrom":subQ1}),1.0]])]});}
            var Q9;
            {var subQ0=sQuery(id+"F6.wireOp",EDGE,"E32");var subQ1=sQuery(id+"F6.wireOp",EDGE,"E13");var subQ2=makeQuery(id+"F6.imprint","INTERSECT",VERTEX,{"disambiguationData":[OD(0.0)],"derivedFrom":[subQ1,subQ0]});Q9=makeQuery(id+"F6.imprint","IMPRINT",FACE,{"disambiguationData":[TD([[makeQuery(id+"F6.imprint","IMPRINT",EDGE,{"disambiguationData":[TD([[subQ2,-1.0]])],"derivedFrom":subQ1}),-1.0]])]});}
            var Q10;
            {var subQ0=sQuery(id+"F6.wireOp",EDGE,"E31");var subQ1=sQuery(id+"F6.wireOp",EDGE,"E13");var subQ2=makeQuery(id+"F6.imprint","INTERSECT",VERTEX,{"disambiguationData":[OD(0.0)],"derivedFrom":[subQ1,subQ0]});Q10=makeQuery(id+"F6.imprint","IMPRINT",FACE,{"disambiguationData":[TD([[makeQuery(id+"F6.imprint","IMPRINT",EDGE,{"disambiguationData":[TD([[subQ2,-1.0]])],"derivedFrom":subQ1}),-1.0]])]});}
            var Q11;
            {var subQ0=sQuery(id+"F6.wireOp",EDGE,"E31");var subQ1=sQuery(id+"F6.wireOp",EDGE,"E13");var subQ2=makeQuery(id+"F6.imprint","INTERSECT",VERTEX,{"disambiguationData":[OD(0.0)],"derivedFrom":[subQ1,subQ0]});Q11=makeQuery(id+"F6.imprint","IMPRINT",FACE,{"disambiguationData":[TD([[makeQuery(id+"F6.imprint","IMPRINT",EDGE,{"disambiguationData":[TD([[subQ2,-1.0]])],"derivedFrom":subQ1}),1.0]])]});}
            extrude(context, id + "F11", {"entities" : qUnion([Q0, Q1, Q2, Q3, Q4, Q5, Q6, Q7, Q8, Q9, Q10, Q11]), "operationType" : NewBodyOperationType.REMOVE, "depth" : 3 * mm, "offsetDistance" : 25 * mm});
        }
        {
            var Q0;
            Q0=qCreatedBy(makeId("Top.planeOp"),FACE);
            var sketch = newSketch(context, id + "F12", { "sketchPlane" : qUnion([Q0])});
            skCircle(sketch, "E37", {"center": v(0, 0) * mm, "radius": 17.33 * mm});
            skSolve(sketch);
        }
        {
            var Q0;
            Q0=makeQuery(id+"F12.imprint","IMPRINT",FACE,{"disambiguationData":[TD([[makeQuery(id+"F12.imprint","IMPRINT",EDGE,{"derivedFrom":sQuery(id+"F12.wireOp",EDGE,"E37")}),1.0]])]});
            extrude(context, id + "F13", {"entities" : qUnion([Q0]), "operationType" : NewBodyOperationType.REMOVE, "depth" : 1 * mm, "offsetDistance" : 25 * mm});
        }
    });
